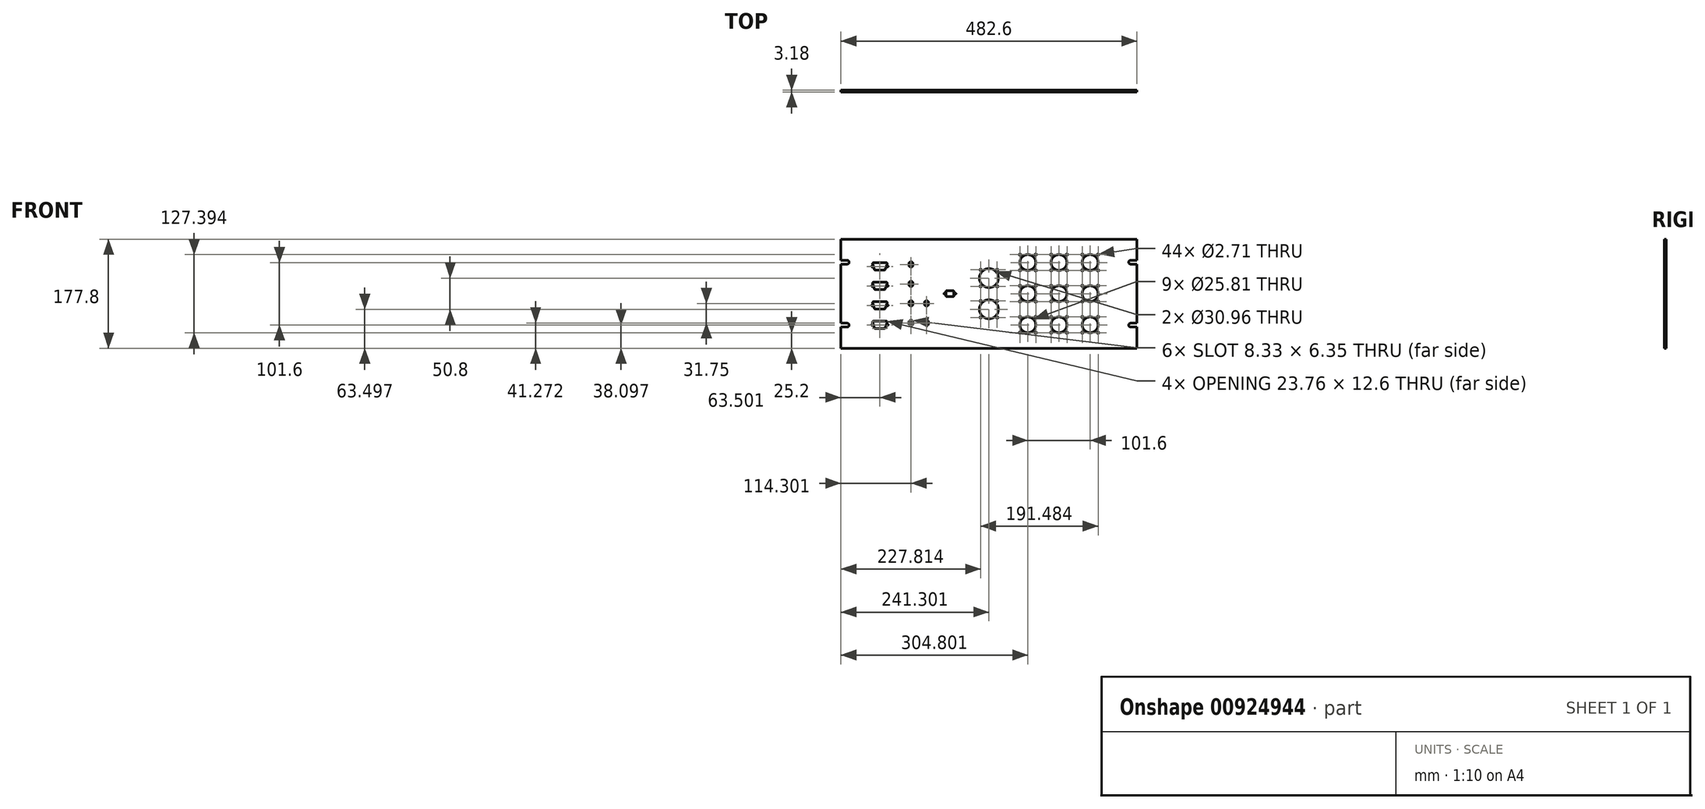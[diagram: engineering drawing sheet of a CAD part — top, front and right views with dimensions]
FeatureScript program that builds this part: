
annotation { "Feature Type Name" : "Feature", "Feature Type Description" : "" }
export const myFeature = defineFeature(function(context is Context, id is Id, definition is map)
    precondition{}
    {
        {
            var Q0;
            Q0=qCreatedBy(makeId("Front.planeOp"),FACE);
            var sketch = newSketch(context, id + "F0", { "sketchPlane" : qUnion([Q0])});
            skLineSegment(sketch, "E0.bottom", {"start": v(-256.05, -152.51) * mm, "end": v(226.55, -152.51) * mm});
            skLineSegment(sketch, "E0.top", {"start": v(-256.05, 25.29) * mm, "end": v(226.55, 25.29) * mm});
            skLineSegment(sketch, "E0.left", {"start": v(-256.05, -152.51) * mm, "end": v(-256.05, -118.1) * mm});
            skLineSegment(sketch, "E0.right", {"start": v(226.55, -152.51) * mm, "end": v(226.55, -118.1) * mm});
            skLineSegment(sketch, "E1", {"start": v(48.75, -99.17) * mm, "end": v(48.75, -129.65) * mm, "construction": true});
            skLineSegment(sketch, "E2", {"start": v(61.45, -114.41) * mm, "end": v(48.75, -114.41) * mm, "construction": true});
            skArc(sketch, "E3", {"start": v(48.75, -101.5) * mm, "mid": v(35.85, -114.41) * mm, "end": v(48.75, -127.32) * mm});
            skPoint(sketch, "E4", {"position": v(36.44, -102.1) * mm});
            skPoint(sketch, "E5", {"position": v(35.26, -100.93) * mm});
            skLineSegment(sketch, "E6", {"start": v(35.26, -100.93) * mm, "end": v(36.44, -102.1) * mm, "construction": true});
            skPoint(sketch, "E7", {"position": v(35.85, -101.52) * mm});
            skPoint(sketch, "E8.MirrorP", {"position": v(61.65, -101.52) * mm});
            skArc(sketch, "E9.MirrorCS", {"start": v(48.75, -101.5) * mm, "mid": v(61.65, -114.41) * mm, "end": v(48.75, -127.32) * mm});
            skPoint(sketch, "E10.MirrorP", {"position": v(35.85, -127.3) * mm});
            skPoint(sketch, "E11.MirrorP", {"position": v(61.65, -127.3) * mm});
            skPoint(sketch, "E12.0.1.0", {"position": v(61.65, -50.72) * mm});
            skLineSegment(sketch, "E12.0.1.1", {"start": v(48.75, -48.37) * mm, "end": v(48.75, -78.85) * mm, "construction": true});
            skPoint(sketch, "E12.0.1.2", {"position": v(36.44, -51.3) * mm});
            skArc(sketch, "E12.0.1.3", {"start": v(48.75, -50.7) * mm, "mid": v(35.85, -63.61) * mm, "end": v(48.75, -76.52) * mm});
            skPoint(sketch, "E12.0.1.4", {"position": v(35.85, -50.72) * mm});
            skArc(sketch, "E12.0.1.5", {"start": v(48.75, -50.7) * mm, "mid": v(61.65, -63.61) * mm, "end": v(48.75, -76.52) * mm});
            skPoint(sketch, "E12.0.1.6", {"position": v(61.65, -76.5) * mm});
            skPoint(sketch, "E12.0.1.7", {"position": v(35.85, -76.5) * mm});
            skLineSegment(sketch, "E12.0.1.8", {"start": v(61.45, -63.61) * mm, "end": v(48.75, -63.61) * mm, "construction": true});
            skPoint(sketch, "E12.0.1.9", {"position": v(35.26, -50.13) * mm});
            skLineSegment(sketch, "E12.0.1.10", {"start": v(35.26, -50.13) * mm, "end": v(36.44, -51.3) * mm, "construction": true});
            skPoint(sketch, "E12.0.2.0", {"position": v(61.65, 0.08) * mm});
            skLineSegment(sketch, "E12.0.2.1", {"start": v(48.75, 2.43) * mm, "end": v(48.75, -28.05) * mm, "construction": true});
            skPoint(sketch, "E12.0.2.2", {"position": v(36.44, -0.5) * mm});
            skArc(sketch, "E12.0.2.3", {"start": v(48.75, 0.1) * mm, "mid": v(35.85, -12.81) * mm, "end": v(48.75, -25.72) * mm});
            skPoint(sketch, "E12.0.2.4", {"position": v(35.85, 0.08) * mm});
            skArc(sketch, "E12.0.2.5", {"start": v(48.75, 0.1) * mm, "mid": v(61.65, -12.81) * mm, "end": v(48.75, -25.72) * mm});
            skPoint(sketch, "E12.0.2.6", {"position": v(61.65, -25.7) * mm});
            skPoint(sketch, "E12.0.2.7", {"position": v(35.85, -25.7) * mm});
            skLineSegment(sketch, "E12.0.2.8", {"start": v(61.45, -12.81) * mm, "end": v(48.75, -12.81) * mm, "construction": true});
            skPoint(sketch, "E12.0.2.9", {"position": v(35.26, 0.67) * mm});
            skLineSegment(sketch, "E12.0.2.10", {"start": v(35.26, 0.67) * mm, "end": v(36.44, -0.5) * mm, "construction": true});
            skPoint(sketch, "E12.1.0.0", {"position": v(112.45, -101.52) * mm});
            skLineSegment(sketch, "E12.1.0.1", {"start": v(99.55, -99.17) * mm, "end": v(99.55, -129.65) * mm, "construction": true});
            skPoint(sketch, "E12.1.0.2", {"position": v(87.24, -102.1) * mm});
            skArc(sketch, "E12.1.0.3", {"start": v(99.55, -101.5) * mm, "mid": v(86.65, -114.41) * mm, "end": v(99.55, -127.32) * mm});
            skPoint(sketch, "E12.1.0.4", {"position": v(86.65, -101.52) * mm});
            skArc(sketch, "E12.1.0.5", {"start": v(99.55, -101.5) * mm, "mid": v(112.45, -114.41) * mm, "end": v(99.55, -127.32) * mm});
            skPoint(sketch, "E12.1.0.6", {"position": v(112.45, -127.3) * mm});
            skPoint(sketch, "E12.1.0.7", {"position": v(86.65, -127.3) * mm});
            skLineSegment(sketch, "E12.1.0.8", {"start": v(112.25, -114.41) * mm, "end": v(99.55, -114.41) * mm, "construction": true});
            skPoint(sketch, "E12.1.0.9", {"position": v(86.06, -100.93) * mm});
            skLineSegment(sketch, "E12.1.0.10", {"start": v(86.06, -100.93) * mm, "end": v(87.24, -102.1) * mm, "construction": true});
            skPoint(sketch, "E12.1.1.0", {"position": v(112.45, -50.72) * mm});
            skLineSegment(sketch, "E12.1.1.1", {"start": v(99.55, -48.37) * mm, "end": v(99.55, -78.85) * mm, "construction": true});
            skPoint(sketch, "E12.1.1.2", {"position": v(87.24, -51.3) * mm});
            skArc(sketch, "E12.1.1.3", {"start": v(99.55, -50.7) * mm, "mid": v(86.65, -63.61) * mm, "end": v(99.55, -76.52) * mm});
            skPoint(sketch, "E12.1.1.4", {"position": v(86.65, -50.72) * mm});
            skArc(sketch, "E12.1.1.5", {"start": v(99.55, -50.7) * mm, "mid": v(112.45, -63.61) * mm, "end": v(99.55, -76.52) * mm});
            skPoint(sketch, "E12.1.1.6", {"position": v(112.45, -76.5) * mm});
            skPoint(sketch, "E12.1.1.7", {"position": v(86.65, -76.5) * mm});
            skLineSegment(sketch, "E12.1.1.8", {"start": v(112.25, -63.61) * mm, "end": v(99.55, -63.61) * mm, "construction": true});
            skPoint(sketch, "E12.1.1.9", {"position": v(86.06, -50.13) * mm});
            skLineSegment(sketch, "E12.1.1.10", {"start": v(86.06, -50.13) * mm, "end": v(87.24, -51.3) * mm, "construction": true});
            skPoint(sketch, "E12.1.2.0", {"position": v(112.45, 0.08) * mm});
            skLineSegment(sketch, "E12.1.2.1", {"start": v(99.55, 2.43) * mm, "end": v(99.55, -28.05) * mm, "construction": true});
            skPoint(sketch, "E12.1.2.2", {"position": v(87.24, -0.5) * mm});
            skArc(sketch, "E12.1.2.3", {"start": v(99.55, 0.1) * mm, "mid": v(86.65, -12.81) * mm, "end": v(99.55, -25.72) * mm});
            skPoint(sketch, "E12.1.2.4", {"position": v(86.65, 0.08) * mm});
            skArc(sketch, "E12.1.2.5", {"start": v(99.55, 0.1) * mm, "mid": v(112.45, -12.81) * mm, "end": v(99.55, -25.72) * mm});
            skPoint(sketch, "E12.1.2.6", {"position": v(112.45, -25.7) * mm});
            skPoint(sketch, "E12.1.2.7", {"position": v(86.65, -25.7) * mm});
            skLineSegment(sketch, "E12.1.2.8", {"start": v(112.25, -12.81) * mm, "end": v(99.55, -12.81) * mm, "construction": true});
            skPoint(sketch, "E12.1.2.9", {"position": v(86.06, 0.67) * mm});
            skLineSegment(sketch, "E12.1.2.10", {"start": v(86.06, 0.67) * mm, "end": v(87.24, -0.5) * mm, "construction": true});
            skPoint(sketch, "E12.2.0.0", {"position": v(163.25, -101.52) * mm});
            skLineSegment(sketch, "E12.2.0.1", {"start": v(150.35, -99.17) * mm, "end": v(150.35, -129.65) * mm, "construction": true});
            skPoint(sketch, "E12.2.0.2", {"position": v(138.04, -102.1) * mm});
            skArc(sketch, "E12.2.0.3", {"start": v(150.35, -101.5) * mm, "mid": v(137.45, -114.41) * mm, "end": v(150.35, -127.32) * mm});
            skPoint(sketch, "E12.2.0.4", {"position": v(137.45, -101.52) * mm});
            skArc(sketch, "E12.2.0.5", {"start": v(150.35, -101.5) * mm, "mid": v(163.25, -114.41) * mm, "end": v(150.35, -127.32) * mm});
            skPoint(sketch, "E12.2.0.6", {"position": v(163.25, -127.3) * mm});
            skPoint(sketch, "E12.2.0.7", {"position": v(137.45, -127.3) * mm});
            skLineSegment(sketch, "E12.2.0.8", {"start": v(163.05, -114.41) * mm, "end": v(150.35, -114.41) * mm, "construction": true});
            skPoint(sketch, "E12.2.0.9", {"position": v(136.86, -100.93) * mm});
            skLineSegment(sketch, "E12.2.0.10", {"start": v(136.86, -100.93) * mm, "end": v(138.04, -102.1) * mm, "construction": true});
            skPoint(sketch, "E12.2.1.0", {"position": v(163.25, -50.72) * mm});
            skLineSegment(sketch, "E12.2.1.1", {"start": v(150.35, -48.37) * mm, "end": v(150.35, -78.85) * mm, "construction": true});
            skPoint(sketch, "E12.2.1.2", {"position": v(138.04, -51.3) * mm});
            skArc(sketch, "E12.2.1.3", {"start": v(150.35, -50.7) * mm, "mid": v(137.45, -63.61) * mm, "end": v(150.35, -76.52) * mm});
            skPoint(sketch, "E12.2.1.4", {"position": v(137.45, -50.72) * mm});
            skArc(sketch, "E12.2.1.5", {"start": v(150.35, -50.7) * mm, "mid": v(163.25, -63.61) * mm, "end": v(150.35, -76.52) * mm});
            skPoint(sketch, "E12.2.1.6", {"position": v(163.25, -76.5) * mm});
            skPoint(sketch, "E12.2.1.7", {"position": v(137.45, -76.5) * mm});
            skLineSegment(sketch, "E12.2.1.8", {"start": v(163.05, -63.61) * mm, "end": v(150.35, -63.61) * mm, "construction": true});
            skPoint(sketch, "E12.2.1.9", {"position": v(136.86, -50.13) * mm});
            skLineSegment(sketch, "E12.2.1.10", {"start": v(136.86, -50.13) * mm, "end": v(138.04, -51.3) * mm, "construction": true});
            skPoint(sketch, "E12.2.2.0", {"position": v(163.25, 0.08) * mm});
            skLineSegment(sketch, "E12.2.2.1", {"start": v(150.35, 2.43) * mm, "end": v(150.35, -28.05) * mm, "construction": true});
            skPoint(sketch, "E12.2.2.2", {"position": v(138.04, -0.5) * mm});
            skArc(sketch, "E12.2.2.3", {"start": v(150.35, 0.1) * mm, "mid": v(137.45, -12.81) * mm, "end": v(150.35, -25.72) * mm});
            skPoint(sketch, "E12.2.2.4", {"position": v(137.45, 0.08) * mm});
            skArc(sketch, "E12.2.2.5", {"start": v(150.35, 0.1) * mm, "mid": v(163.25, -12.81) * mm, "end": v(150.35, -25.72) * mm});
            skPoint(sketch, "E12.2.2.6", {"position": v(163.25, -25.7) * mm});
            skPoint(sketch, "E12.2.2.7", {"position": v(137.45, -25.7) * mm});
            skLineSegment(sketch, "E12.2.2.8", {"start": v(163.05, -12.81) * mm, "end": v(150.35, -12.81) * mm, "construction": true});
            skPoint(sketch, "E12.2.2.9", {"position": v(136.86, 0.67) * mm});
            skLineSegment(sketch, "E12.2.2.10", {"start": v(136.86, 0.67) * mm, "end": v(138.04, -0.5) * mm, "construction": true});
            skLineSegment(sketch, "E12.direction1", {"start": v(35.85, -127.3) * mm, "end": v(86.65, -127.3) * mm, "construction": true});
            skLineSegment(sketch, "E12.direction2", {"start": v(35.85, -127.3) * mm, "end": v(35.85, -76.5) * mm, "construction": true});
            skPoint(sketch, "E13", {"position": v(-245.76, -12.3) * mm});
            skLineSegment(sketch, "E14", {"start": v(-256.05, -63.61) * mm, "end": v(-239.44, -63.61) * mm, "construction": true});
            skLineSegment(sketch, "E15", {"start": v(-14.75, 38.2) * mm, "end": v(-14.75, 25.29) * mm, "construction": true});
            skLineSegment(sketch, "E16", {"start": v(-245.76, -12.3) * mm, "end": v(-256.05, -12.3) * mm, "construction": true});
            skArc(sketch, "E17.0.startCap", {"start": v(-245.76, -9.13) * mm, "mid": v(-242.59, -12.3) * mm, "end": v(-245.76, -15.48) * mm});
            skLineSegment(sketch, "E17.0.left", {"start": v(-245.76, -15.48) * mm, "end": v(-256.05, -15.48) * mm});
            skLineSegment(sketch, "E17.0.right", {"start": v(-245.76, -9.13) * mm, "end": v(-256.05, -9.13) * mm});
            skLineSegment(sketch, "E18.trimOffspring", {"start": v(-256.05, -9.13) * mm, "end": v(-256.05, 25.29) * mm});
            skArc(sketch, "E19.MirrorCS", {"start": v(-245.76, -118.1) * mm, "mid": v(-242.59, -114.92) * mm, "end": v(-245.76, -111.75) * mm});
            skLineSegment(sketch, "E20.MirrorCS", {"start": v(-245.76, -111.75) * mm, "end": v(-256.05, -111.75) * mm});
            skLineSegment(sketch, "E21.MirrorCS", {"start": v(-256.05, -118.1) * mm, "end": v(-256.05, -152.51) * mm});
            skLineSegment(sketch, "E22.MirrorCS", {"start": v(-245.76, -118.1) * mm, "end": v(-256.05, -118.1) * mm});
            skLineSegment(sketch, "E23.trimOffspring", {"start": v(-256.05, -111.75) * mm, "end": v(-256.05, -15.48) * mm});
            skArc(sketch, "E24.MirrorCS", {"start": v(216.26, -9.13) * mm, "mid": v(213.09, -12.3) * mm, "end": v(216.26, -15.48) * mm});
            skLineSegment(sketch, "E25.MirrorCS", {"start": v(216.26, -15.48) * mm, "end": v(226.55, -15.48) * mm});
            skLineSegment(sketch, "E26.MirrorCS", {"start": v(216.26, -9.13) * mm, "end": v(226.55, -9.13) * mm});
            skLineSegment(sketch, "E27.MirrorCS", {"start": v(216.26, -111.75) * mm, "end": v(226.55, -111.75) * mm});
            skArc(sketch, "E28.MirrorCS", {"start": v(216.26, -118.1) * mm, "mid": v(213.09, -114.92) * mm, "end": v(216.26, -111.75) * mm});
            skLineSegment(sketch, "E29.MirrorCS", {"start": v(216.26, -118.1) * mm, "end": v(226.55, -118.1) * mm});
            skLineSegment(sketch, "E30.trimOffspring", {"start": v(226.55, -9.13) * mm, "end": v(226.55, 25.29) * mm});
            skLineSegment(sketch, "E31.trimOffspring", {"start": v(226.55, -111.75) * mm, "end": v(226.55, -15.48) * mm});
            skLineSegment(sketch, "E32", {"start": v(-205.05, -114.41) * mm, "end": v(-180.05, -114.41) * mm, "construction": true});
            skLineSegment(sketch, "E33", {"start": v(-192.55, -118.22) * mm, "end": v(-192.55, -110.6) * mm, "construction": true});
            skPoint(sketch, "E33.startSnap0", {"position": v(-192.55, -114.41) * mm});
            skLineSegment(sketch, "E34", {"start": v(-192.55, -106.3) * mm, "end": v(-192.55, -106.3) * mm});
            skLineSegment(sketch, "E35", {"start": v(-192.55, -118) * mm, "end": v(-192.55, -118) * mm});
            skLineSegment(sketch, "E36", {"start": v(-204.33, -110.87) * mm, "end": v(-201.61, -119.26) * mm});
            skLineSegment(sketch, "E37", {"start": v(-180.76, -110.87) * mm, "end": v(-183.49, -119.26) * mm});
            skLineSegment(sketch, "E38", {"start": v(-202.33, -108.11) * mm, "end": v(-182.77, -108.11) * mm});
            skLineSegment(sketch, "E39", {"start": v(-199.6, -120.71) * mm, "end": v(-185.5, -120.71) * mm});
            skLineSegment(sketch, "E40", {"start": v(-192.55, -108.11) * mm, "end": v(-192.55, -104.89) * mm, "construction": true});
            skLineSegment(sketch, "E41", {"start": v(-192.55, -120.71) * mm, "end": v(-192.55, -122.22) * mm, "construction": true});
            skArc(sketch, "E42", {"start": v(-202.33, -108.11) * mm, "mid": v(-204.03, -108.98) * mm, "end": v(-204.33, -110.87) * mm});
            skArc(sketch, "E43", {"start": v(-180.76, -110.87) * mm, "mid": v(-181.06, -108.98) * mm, "end": v(-182.77, -108.11) * mm});
            skArc(sketch, "E44", {"start": v(-185.5, -120.71) * mm, "mid": v(-184.25, -120.3) * mm, "end": v(-183.49, -119.26) * mm});
            skArc(sketch, "E45", {"start": v(-201.61, -119.26) * mm, "mid": v(-200.85, -120.3) * mm, "end": v(-199.6, -120.71) * mm});
            skLineSegment(sketch, "E46.direction1", {"start": v(-188.91, -123.4) * mm, "end": v(-163.51, -123.4) * mm, "construction": true});
            skLineSegment(sketch, "E46.direction2", {"start": v(-188.91, -123.4) * mm, "end": v(-188.91, -91.66) * mm, "construction": true});
            skArc(sketch, "E47", {"start": v(-138.57, -108.54) * mm, "mid": v(-141.75, -107.07) * mm, "end": v(-144.92, -108.54) * mm});
            skLineSegment(sketch, "E48.left", {"start": v(-138.57, -113.93) * mm, "end": v(-138.57, -108.54) * mm});
            skLineSegment(sketch, "E48.right", {"start": v(-144.92, -113.93) * mm, "end": v(-144.92, -108.54) * mm});
            skArc(sketch, "E49.trimOffspring", {"start": v(-144.92, -113.93) * mm, "mid": v(-141.75, -115.4) * mm, "end": v(-138.57, -113.93) * mm});
            skArc(sketch, "E50.0.1.0", {"start": v(-138.57, -76.8) * mm, "mid": v(-141.75, -75.32) * mm, "end": v(-144.92, -76.8) * mm});
            skArc(sketch, "E50.0.1.1", {"start": v(-144.92, -82.18) * mm, "mid": v(-141.75, -83.65) * mm, "end": v(-138.57, -82.18) * mm});
            skPoint(sketch, "E50.0.1.2", {"position": v(-141.75, -79.49) * mm});
            skLineSegment(sketch, "E50.0.1.3", {"start": v(-138.57, -82.18) * mm, "end": v(-138.57, -76.8) * mm});
            skLineSegment(sketch, "E50.0.1.4", {"start": v(-144.92, -82.18) * mm, "end": v(-144.92, -76.8) * mm});
            skArc(sketch, "E50.0.2.0", {"start": v(-138.57, -45.04) * mm, "mid": v(-141.75, -43.57) * mm, "end": v(-144.92, -45.04) * mm});
            skArc(sketch, "E50.0.2.1", {"start": v(-144.92, -50.43) * mm, "mid": v(-141.75, -51.9) * mm, "end": v(-138.57, -50.43) * mm});
            skPoint(sketch, "E50.0.2.2", {"position": v(-141.75, -47.74) * mm});
            skLineSegment(sketch, "E50.0.2.3", {"start": v(-138.57, -50.43) * mm, "end": v(-138.57, -45.04) * mm});
            skLineSegment(sketch, "E50.0.2.4", {"start": v(-144.92, -50.43) * mm, "end": v(-144.92, -45.04) * mm});
            skArc(sketch, "E50.0.3.0", {"start": v(-138.57, -13.3) * mm, "mid": v(-141.75, -11.82) * mm, "end": v(-144.92, -13.3) * mm});
            skArc(sketch, "E50.0.3.1", {"start": v(-144.92, -18.68) * mm, "mid": v(-141.75, -20.15) * mm, "end": v(-138.57, -18.68) * mm});
            skPoint(sketch, "E50.0.3.2", {"position": v(-141.75, -15.99) * mm});
            skLineSegment(sketch, "E50.0.3.3", {"start": v(-138.57, -18.68) * mm, "end": v(-138.57, -13.3) * mm});
            skLineSegment(sketch, "E50.0.3.4", {"start": v(-144.92, -18.68) * mm, "end": v(-144.92, -13.3) * mm});
            skLineSegment(sketch, "E50.direction1", {"start": v(-144.92, -113.93) * mm, "end": v(-119.52, -113.93) * mm, "construction": true});
            skLineSegment(sketch, "E50.direction2", {"start": v(-144.92, -113.93) * mm, "end": v(-144.92, -82.18) * mm, "construction": true});
            skLineSegment(sketch, "E51", {"start": v(-141.75, -47.74) * mm, "end": v(-141.75, -79.49) * mm, "construction": true});
            skLineSegment(sketch, "E52", {"start": v(-141.75, -63.61) * mm, "end": v(-151.51, -63.61) * mm, "construction": true});
            skLineSegment(sketch, "E53.0.0.1", {"start": v(-199.6, -88.96) * mm, "end": v(-185.5, -88.96) * mm});
            skLineSegment(sketch, "E53.3.0.1", {"start": v(-180.76, -79.12) * mm, "end": v(-183.49, -87.5) * mm});
            skArc(sketch, "E53.6.0.1", {"start": v(-202.33, -76.36) * mm, "mid": v(-204.03, -77.23) * mm, "end": v(-204.33, -79.12) * mm});
            skLineSegment(sketch, "E53.10.0.1", {"start": v(-205.05, -82.66) * mm, "end": v(-180.05, -82.66) * mm, "construction": true});
            skLineSegment(sketch, "E53.13.0.1", {"start": v(-202.33, -76.36) * mm, "end": v(-182.77, -76.36) * mm});
            skArc(sketch, "E53.16.0.1", {"start": v(-180.76, -79.12) * mm, "mid": v(-181.06, -77.23) * mm, "end": v(-182.77, -76.36) * mm});
            skLineSegment(sketch, "E53.20.0.1", {"start": v(-204.33, -79.12) * mm, "end": v(-201.61, -87.5) * mm});
            skLineSegment(sketch, "E53.23.0.1", {"start": v(-192.55, -76.36) * mm, "end": v(-192.55, -73.14) * mm, "construction": true});
            skLineSegment(sketch, "E53.26.0.1", {"start": v(-192.55, -86.47) * mm, "end": v(-192.55, -78.85) * mm, "construction": true});
            skPoint(sketch, "E53.29.0.1", {"position": v(-192.55, -82.66) * mm});
            skArc(sketch, "E53.30.0.1", {"start": v(-185.5, -88.96) * mm, "mid": v(-184.25, -88.56) * mm, "end": v(-183.49, -87.5) * mm});
            skLineSegment(sketch, "E53.34.0.1", {"start": v(-192.55, -88.96) * mm, "end": v(-192.55, -90.47) * mm, "construction": true});
            skArc(sketch, "E53.37.0.1", {"start": v(-201.61, -87.5) * mm, "mid": v(-200.85, -88.56) * mm, "end": v(-199.6, -88.96) * mm});
            skLineSegment(sketch, "E53.0.0.2", {"start": v(-199.6, -57.21) * mm, "end": v(-185.5, -57.21) * mm});
            skLineSegment(sketch, "E53.3.0.2", {"start": v(-180.76, -47.37) * mm, "end": v(-183.49, -55.76) * mm});
            skArc(sketch, "E53.6.0.2", {"start": v(-202.33, -44.61) * mm, "mid": v(-204.03, -45.48) * mm, "end": v(-204.33, -47.37) * mm});
            skLineSegment(sketch, "E53.10.0.2", {"start": v(-205.05, -50.91) * mm, "end": v(-180.05, -50.91) * mm, "construction": true});
            skLineSegment(sketch, "E53.13.0.2", {"start": v(-202.33, -44.61) * mm, "end": v(-182.77, -44.61) * mm});
            skArc(sketch, "E53.16.0.2", {"start": v(-180.76, -47.37) * mm, "mid": v(-181.06, -45.48) * mm, "end": v(-182.77, -44.61) * mm});
            skLineSegment(sketch, "E53.20.0.2", {"start": v(-204.33, -47.37) * mm, "end": v(-201.61, -55.76) * mm});
            skLineSegment(sketch, "E53.23.0.2", {"start": v(-192.55, -44.61) * mm, "end": v(-192.55, -41.39) * mm, "construction": true});
            skLineSegment(sketch, "E53.26.0.2", {"start": v(-192.55, -54.72) * mm, "end": v(-192.55, -47.1) * mm, "construction": true});
            skPoint(sketch, "E53.29.0.2", {"position": v(-192.55, -50.91) * mm});
            skArc(sketch, "E53.30.0.2", {"start": v(-185.5, -57.21) * mm, "mid": v(-184.25, -56.8) * mm, "end": v(-183.49, -55.76) * mm});
            skLineSegment(sketch, "E53.34.0.2", {"start": v(-192.55, -57.21) * mm, "end": v(-192.55, -58.72) * mm, "construction": true});
            skArc(sketch, "E53.37.0.2", {"start": v(-201.61, -55.76) * mm, "mid": v(-200.85, -56.8) * mm, "end": v(-199.6, -57.21) * mm});
            skLineSegment(sketch, "E53.0.0.3", {"start": v(-199.6, -25.46) * mm, "end": v(-185.5, -25.46) * mm});
            skLineSegment(sketch, "E53.3.0.3", {"start": v(-180.76, -15.62) * mm, "end": v(-183.49, -24) * mm});
            skArc(sketch, "E53.6.0.3", {"start": v(-202.33, -12.86) * mm, "mid": v(-204.03, -13.73) * mm, "end": v(-204.33, -15.62) * mm});
            skLineSegment(sketch, "E53.10.0.3", {"start": v(-205.05, -19.16) * mm, "end": v(-180.05, -19.16) * mm, "construction": true});
            skLineSegment(sketch, "E53.13.0.3", {"start": v(-202.33, -12.86) * mm, "end": v(-182.77, -12.86) * mm});
            skArc(sketch, "E53.16.0.3", {"start": v(-180.76, -15.62) * mm, "mid": v(-181.06, -13.73) * mm, "end": v(-182.77, -12.86) * mm});
            skLineSegment(sketch, "E53.20.0.3", {"start": v(-204.33, -15.62) * mm, "end": v(-201.61, -24) * mm});
            skLineSegment(sketch, "E53.23.0.3", {"start": v(-192.55, -12.86) * mm, "end": v(-192.55, -9.64) * mm, "construction": true});
            skLineSegment(sketch, "E53.26.0.3", {"start": v(-192.55, -22.97) * mm, "end": v(-192.55, -15.35) * mm, "construction": true});
            skPoint(sketch, "E53.29.0.3", {"position": v(-192.55, -19.16) * mm});
            skArc(sketch, "E53.30.0.3", {"start": v(-185.5, -25.46) * mm, "mid": v(-184.25, -25.06) * mm, "end": v(-183.49, -24) * mm});
            skLineSegment(sketch, "E53.34.0.3", {"start": v(-192.55, -25.46) * mm, "end": v(-192.55, -26.97) * mm, "construction": true});
            skArc(sketch, "E53.37.0.3", {"start": v(-201.61, -24) * mm, "mid": v(-200.85, -25.06) * mm, "end": v(-199.6, -25.46) * mm});
            skLineSegment(sketch, "E54.bottom", {"start": v(-1.26, -102.5) * mm, "end": v(-28.24, -102.5) * mm, "construction": true});
            skLineSegment(sketch, "E54.top", {"start": v(-1.26, -75.53) * mm, "end": v(-28.24, -75.53) * mm, "construction": true});
            skLineSegment(sketch, "E54.left", {"start": v(-1.26, -102.5) * mm, "end": v(-1.26, -75.53) * mm, "construction": true});
            skLineSegment(sketch, "E54.right", {"start": v(-28.24, -102.5) * mm, "end": v(-28.24, -75.53) * mm, "construction": true});
            skPoint(sketch, "E54.middle", {"position": v(-14.75, -89.01) * mm});
            skCircle(sketch, "E55", {"center": v(-14.75, -89.01) * mm, "radius": 15.48 * mm});
            skCircle(sketch, "E56.0.1.0", {"center": v(-14.75, -38.21) * mm, "radius": 15.48 * mm});
            skPoint(sketch, "E56.0.1.1", {"position": v(-14.75, -38.21) * mm});
            skLineSegment(sketch, "E56.0.1.2", {"start": v(-28.24, -51.7) * mm, "end": v(-28.24, -24.73) * mm, "construction": true});
            skLineSegment(sketch, "E56.0.1.3", {"start": v(-1.26, -51.7) * mm, "end": v(-1.26, -24.73) * mm, "construction": true});
            skLineSegment(sketch, "E56.0.1.4", {"start": v(-1.26, -51.7) * mm, "end": v(-28.24, -51.7) * mm, "construction": true});
            skLineSegment(sketch, "E56.0.1.5", {"start": v(-1.26, -24.73) * mm, "end": v(-28.24, -24.73) * mm, "construction": true});
            skLineSegment(sketch, "E56.direction1", {"start": v(-80.15, -102.5) * mm, "end": v(-28.24, -102.5) * mm, "construction": true});
            skLineSegment(sketch, "E56.direction2", {"start": v(-28.24, -102.5) * mm, "end": v(-28.24, -51.7) * mm, "construction": true});
            skLineSegment(sketch, "E57", {"start": v(-14.75, -38.21) * mm, "end": v(-14.75, -89.01) * mm, "construction": true});
            skLineSegment(sketch, "E58", {"start": v(-12.7, -63.61) * mm, "end": v(-14.75, -63.61) * mm, "construction": true});
            skLineSegment(sketch, "E59.bottom", {"start": v(-72.25, -68.36) * mm, "end": v(-84.24, -68.36) * mm});
            skLineSegment(sketch, "E59.top", {"start": v(-72.25, -58.86) * mm, "end": v(-84.24, -58.86) * mm});
            skLineSegment(sketch, "E59.left", {"start": v(-71.75, -67.85) * mm, "end": v(-71.75, -59.37) * mm});
            skLineSegment(sketch, "E59.right", {"start": v(-84.75, -67.85) * mm, "end": v(-84.75, -59.37) * mm});
            skPoint(sketch, "E59.middle", {"position": v(-78.25, -63.61) * mm});
            skLineSegment(sketch, "E60", {"start": v(-87.25, -63.61) * mm, "end": v(-69.24, -63.61) * mm, "construction": true});
            skPoint(sketch, "E61.visualSharp", {"position": v(-84.75, -58.86) * mm});
            skArc(sketch, "E61.filletArc", {"start": v(-84.24, -58.86) * mm, "mid": v(-84.6, -59.01) * mm, "end": v(-84.75, -59.37) * mm});
            skPoint(sketch, "E62.visualSharp", {"position": v(-71.75, -58.86) * mm});
            skArc(sketch, "E62.filletArc", {"start": v(-71.75, -59.37) * mm, "mid": v(-71.9, -59.01) * mm, "end": v(-72.25, -58.86) * mm});
            skPoint(sketch, "E63.visualSharp", {"position": v(-71.75, -68.36) * mm});
            skArc(sketch, "E63.filletArc", {"start": v(-72.25, -68.36) * mm, "mid": v(-71.9, -68.21) * mm, "end": v(-71.75, -67.85) * mm});
            skPoint(sketch, "E64.visualSharp", {"position": v(-84.75, -68.36) * mm});
            skArc(sketch, "E64.filletArc", {"start": v(-84.75, -67.85) * mm, "mid": v(-84.6, -68.21) * mm, "end": v(-84.24, -68.36) * mm});
            skArc(sketch, "E65.0.1.0", {"start": v(-113.17, -108.54) * mm, "mid": v(-116.35, -107.07) * mm, "end": v(-119.52, -108.54) * mm});
            skArc(sketch, "E65.4.1.0", {"start": v(-119.52, -113.93) * mm, "mid": v(-116.35, -115.4) * mm, "end": v(-113.17, -113.93) * mm});
            skPoint(sketch, "E65.8.1.0", {"position": v(-116.35, -111.24) * mm});
            skLineSegment(sketch, "E65.9.1.0", {"start": v(-113.17, -113.93) * mm, "end": v(-113.17, -108.54) * mm});
            skLineSegment(sketch, "E65.12.1.0", {"start": v(-119.52, -113.93) * mm, "end": v(-119.52, -108.54) * mm});
            skArc(sketch, "E65.0.1.1", {"start": v(-113.17, -76.8) * mm, "mid": v(-116.35, -75.32) * mm, "end": v(-119.52, -76.8) * mm});
            skArc(sketch, "E65.4.1.1", {"start": v(-119.52, -82.18) * mm, "mid": v(-116.35, -83.65) * mm, "end": v(-113.17, -82.18) * mm});
            skPoint(sketch, "E65.8.1.1", {"position": v(-116.35, -79.49) * mm});
            skLineSegment(sketch, "E65.9.1.1", {"start": v(-113.17, -82.18) * mm, "end": v(-113.17, -76.8) * mm});
            skLineSegment(sketch, "E65.12.1.1", {"start": v(-119.52, -82.18) * mm, "end": v(-119.52, -76.8) * mm});
            skSolve(sketch);
        }
        {
            var Q0;
            Q0=qSketchRegion(id+"F0",true);
            extrude(context, id + "F1", {"entities" : qUnion([Q0]), "depth" : 3.17 * mm, "offsetDistance" : 25.4 * mm});
        }
        {
            var Q0;
            Q0=sQuery(id+"F0.wireOp",VERTEX,"E12.0.2.4");
            var Q1;
            Q1=sQuery(id+"F0.wireOp",VERTEX,"E12.0.2.0");
            var Q2;
            Q2=sQuery(id+"F0.wireOp",VERTEX,"E12.0.2.6");
            var Q3;
            Q3=sQuery(id+"F0.wireOp",VERTEX,"E12.0.2.7");
            var Q4;
            Q4=sQuery(id+"F0.wireOp",VERTEX,"E12.1.2.7");
            var Q5;
            Q5=sQuery(id+"F0.wireOp",VERTEX,"E12.1.2.6");
            var Q6;
            Q6=sQuery(id+"F0.wireOp",VERTEX,"E12.1.2.0");
            var Q7;
            Q7=sQuery(id+"F0.wireOp",VERTEX,"E12.1.2.4");
            var Q8;
            Q8=sQuery(id+"F0.wireOp",VERTEX,"E12.0.1.4");
            var Q9;
            Q9=sQuery(id+"F0.wireOp",VERTEX,"E12.0.1.0");
            var Q10;
            Q10=sQuery(id+"F0.wireOp",VERTEX,"E12.1.1.4");
            var Q11;
            Q11=sQuery(id+"F0.wireOp",VERTEX,"E12.1.1.0");
            var Q12;
            Q12=sQuery(id+"F0.wireOp",VERTEX,"E12.2.2.4");
            var Q13;
            Q13=sQuery(id+"F0.wireOp",VERTEX,"E12.2.2.0");
            var Q14;
            Q14=sQuery(id+"F0.wireOp",VERTEX,"E12.2.2.6");
            var Q15;
            Q15=sQuery(id+"F0.wireOp",VERTEX,"E12.2.2.7");
            var Q16;
            Q16=sQuery(id+"F0.wireOp",VERTEX,"E12.2.1.4");
            var Q17;
            Q17=sQuery(id+"F0.wireOp",VERTEX,"E12.2.1.0");
            var Q18;
            Q18=sQuery(id+"F0.wireOp",VERTEX,"E12.0.1.7");
            var Q19;
            Q19=sQuery(id+"F0.wireOp",VERTEX,"E12.0.1.6");
            var Q20;
            Q20=sQuery(id+"F0.wireOp",VERTEX,"E12.1.1.7");
            var Q21;
            Q21=sQuery(id+"F0.wireOp",VERTEX,"E12.1.1.6");
            var Q22;
            Q22=sQuery(id+"F0.wireOp",VERTEX,"E12.2.1.7");
            var Q23;
            Q23=sQuery(id+"F0.wireOp",VERTEX,"E12.2.1.6");
            var Q24;
            Q24=sQuery(id+"F0.wireOp",VERTEX,"E12.2.0.0");
            var Q25;
            Q25=sQuery(id+"F0.wireOp",VERTEX,"E12.2.0.4");
            var Q26;
            Q26=sQuery(id+"F0.wireOp",VERTEX,"E12.1.0.0");
            var Q27;
            Q27=sQuery(id+"F0.wireOp",VERTEX,"E12.1.0.4");
            var Q28;
            Q28=sQuery(id+"F0.wireOp",VERTEX,"E8.MirrorP");
            var Q29;
            Q29=sQuery(id+"F0.wireOp",VERTEX,"E7");
            var Q30;
            Q30=sQuery(id+"F0.wireOp",VERTEX,"E10.MirrorP");
            var Q31;
            Q31=sQuery(id+"F0.wireOp",VERTEX,"E11.MirrorP");
            var Q32;
            Q32=sQuery(id+"F0.wireOp",VERTEX,"E12.1.0.7");
            var Q33;
            Q33=sQuery(id+"F0.wireOp",VERTEX,"E12.1.0.6");
            var Q34;
            Q34=sQuery(id+"F0.wireOp",VERTEX,"E12.2.0.7");
            var Q35;
            Q35=sQuery(id+"F0.wireOp",VERTEX,"E12.2.0.6");
            var Q36;
            Q36=makeQuery(id+"F1.opExtrude","SWEPT_BODY",BODY,{"disambiguationData":[OSD([sQuery(id+"F0.wireOp",EDGE,"E0.bottom"),sQuery(id+"F0.wireOp",EDGE,"E0.top"),sQuery(id+"F0.wireOp",EDGE,"E0.left"),sQuery(id+"F0.wireOp",EDGE,"E0.right"),sQuery(id+"F0.wireOp",EDGE,"b0d6a3e9-dda7-4b39-bde3-1ef797a92e78"),sQuery(id+"F0.wireOp",EDGE,"de29c7d1-a9bf-4cad-87a4-eb185ccb766c"),sQuery(id+"F0.wireOp",EDGE,"d8eac7f8-13a5-4df2-9675-793bb3d629a8"),sQuery(id+"F0.wireOp",EDGE,"9a60e7e6-8b1c-49ce-a587-7fef7e458512"),sQuery(id+"F0.wireOp",EDGE,"f7618abf-457f-4771-8f9e-37748c564853"),sQuery(id+"F0.wireOp",EDGE,"12616632-bdf5-4fef-91ed-fab7e749e060"),sQuery(id+"F0.wireOp",EDGE,"a72d509d-39ea-4c83-8068-937b1f15b5a1"),sQuery(id+"F0.wireOp",EDGE,"b72412ee-4e9a-4b00-b16c-6c6999a1730f"),sQuery(id+"F0.wireOp",EDGE,"7d2e699d-989a-44b9-9e27-5967113c99a9"),sQuery(id+"F0.wireOp",EDGE,"4471e13d-aa83-4026-a50f-020390fa38f4"),sQuery(id+"F0.wireOp",EDGE,"1e7b34f2-0b9f-4ddf-89ed-3da1b662023f.0.1.1"),sQuery(id+"F0.wireOp",EDGE,"1e7b34f2-0b9f-4ddf-89ed-3da1b662023f.0.1.2"),sQuery(id+"F0.wireOp",EDGE,"1e7b34f2-0b9f-4ddf-89ed-3da1b662023f.0.1.3"),sQuery(id+"F0.wireOp",EDGE,"1e7b34f2-0b9f-4ddf-89ed-3da1b662023f.0.1.4"),sQuery(id+"F0.wireOp",EDGE,"1e7b34f2-0b9f-4ddf-89ed-3da1b662023f.0.1.8"),sQuery(id+"F0.wireOp",EDGE,"1e7b34f2-0b9f-4ddf-89ed-3da1b662023f.0.1.12"),sQuery(id+"F0.wireOp",EDGE,"1e7b34f2-0b9f-4ddf-89ed-3da1b662023f.0.1.13"),sQuery(id+"F0.wireOp",EDGE,"1e7b34f2-0b9f-4ddf-89ed-3da1b662023f.0.1.14"),sQuery(id+"F0.wireOp",EDGE,"1e7b34f2-0b9f-4ddf-89ed-3da1b662023f.0.1.15"),sQuery(id+"F0.wireOp",EDGE,"1e7b34f2-0b9f-4ddf-89ed-3da1b662023f.0.1.16"),sQuery(id+"F0.wireOp",EDGE,"1e7b34f2-0b9f-4ddf-89ed-3da1b662023f.0.2.1"),sQuery(id+"F0.wireOp",EDGE,"1e7b34f2-0b9f-4ddf-89ed-3da1b662023f.0.2.2"),sQuery(id+"F0.wireOp",EDGE,"1e7b34f2-0b9f-4ddf-89ed-3da1b662023f.0.2.3"),sQuery(id+"F0.wireOp",EDGE,"1e7b34f2-0b9f-4ddf-89ed-3da1b662023f.0.2.4"),sQuery(id+"F0.wireOp",EDGE,"1e7b34f2-0b9f-4ddf-89ed-3da1b662023f.0.2.8"),sQuery(id+"F0.wireOp",EDGE,"1e7b34f2-0b9f-4ddf-89ed-3da1b662023f.0.2.12"),sQuery(id+"F0.wireOp",EDGE,"1e7b34f2-0b9f-4ddf-89ed-3da1b662023f.0.2.13"),sQuery(id+"F0.wireOp",EDGE,"1e7b34f2-0b9f-4ddf-89ed-3da1b662023f.0.2.14"),sQuery(id+"F0.wireOp",EDGE,"1e7b34f2-0b9f-4ddf-89ed-3da1b662023f.0.2.15"),sQuery(id+"F0.wireOp",EDGE,"1e7b34f2-0b9f-4ddf-89ed-3da1b662023f.0.2.16"),sQuery(id+"F0.wireOp",EDGE,"1e7b34f2-0b9f-4ddf-89ed-3da1b662023f.0.3.1"),sQuery(id+"F0.wireOp",EDGE,"1e7b34f2-0b9f-4ddf-89ed-3da1b662023f.0.3.2"),sQuery(id+"F0.wireOp",EDGE,"1e7b34f2-0b9f-4ddf-89ed-3da1b662023f.0.3.3"),sQuery(id+"F0.wireOp",EDGE,"1e7b34f2-0b9f-4ddf-89ed-3da1b662023f.0.3.4"),sQuery(id+"F0.wireOp",EDGE,"1e7b34f2-0b9f-4ddf-89ed-3da1b662023f.0.3.8"),sQuery(id+"F0.wireOp",EDGE,"1e7b34f2-0b9f-4ddf-89ed-3da1b662023f.0.3.12"),sQuery(id+"F0.wireOp",EDGE,"1e7b34f2-0b9f-4ddf-89ed-3da1b662023f.0.3.13"),sQuery(id+"F0.wireOp",EDGE,"1e7b34f2-0b9f-4ddf-89ed-3da1b662023f.0.3.14"),sQuery(id+"F0.wireOp",EDGE,"1e7b34f2-0b9f-4ddf-89ed-3da1b662023f.0.3.15"),sQuery(id+"F0.wireOp",EDGE,"1e7b34f2-0b9f-4ddf-89ed-3da1b662023f.0.3.16"),sQuery(id+"F0.wireOp",EDGE,"1e7b34f2-0b9f-4ddf-89ed-3da1b662023f.0.4.1"),sQuery(id+"F0.wireOp",EDGE,"1e7b34f2-0b9f-4ddf-89ed-3da1b662023f.0.4.2"),sQuery(id+"F0.wireOp",EDGE,"1e7b34f2-0b9f-4ddf-89ed-3da1b662023f.0.4.3"),sQuery(id+"F0.wireOp",EDGE,"1e7b34f2-0b9f-4ddf-89ed-3da1b662023f.0.4.4"),sQuery(id+"F0.wireOp",EDGE,"1e7b34f2-0b9f-4ddf-89ed-3da1b662023f.0.4.8"),sQuery(id+"F0.wireOp",EDGE,"1e7b34f2-0b9f-4ddf-89ed-3da1b662023f.0.4.12"),sQuery(id+"F0.wireOp",EDGE,"1e7b34f2-0b9f-4ddf-89ed-3da1b662023f.0.4.13"),sQuery(id+"F0.wireOp",EDGE,"1e7b34f2-0b9f-4ddf-89ed-3da1b662023f.0.4.14"),sQuery(id+"F0.wireOp",EDGE,"1e7b34f2-0b9f-4ddf-89ed-3da1b662023f.0.4.15"),sQuery(id+"F0.wireOp",EDGE,"1e7b34f2-0b9f-4ddf-89ed-3da1b662023f.0.4.16"),sQuery(id+"F0.wireOp",EDGE,"1e7b34f2-0b9f-4ddf-89ed-3da1b662023f.0.5.1"),sQuery(id+"F0.wireOp",EDGE,"1e7b34f2-0b9f-4ddf-89ed-3da1b662023f.0.5.2"),sQuery(id+"F0.wireOp",EDGE,"1e7b34f2-0b9f-4ddf-89ed-3da1b662023f.0.5.3"),sQuery(id+"F0.wireOp",EDGE,"1e7b34f2-0b9f-4ddf-89ed-3da1b662023f.0.5.4"),sQuery(id+"F0.wireOp",EDGE,"1e7b34f2-0b9f-4ddf-89ed-3da1b662023f.0.5.8"),sQuery(id+"F0.wireOp",EDGE,"1e7b34f2-0b9f-4ddf-89ed-3da1b662023f.0.5.12"),sQuery(id+"F0.wireOp",EDGE,"1e7b34f2-0b9f-4ddf-89ed-3da1b662023f.0.5.13"),sQuery(id+"F0.wireOp",EDGE,"1e7b34f2-0b9f-4ddf-89ed-3da1b662023f.0.5.14"),sQuery(id+"F0.wireOp",EDGE,"1e7b34f2-0b9f-4ddf-89ed-3da1b662023f.0.5.15"),sQuery(id+"F0.wireOp",EDGE,"1e7b34f2-0b9f-4ddf-89ed-3da1b662023f.0.5.16"),sQuery(id+"F0.wireOp",EDGE,"1e7b34f2-0b9f-4ddf-89ed-3da1b662023f.0.6.1"),sQuery(id+"F0.wireOp",EDGE,"1e7b34f2-0b9f-4ddf-89ed-3da1b662023f.0.6.2"),sQuery(id+"F0.wireOp",EDGE,"1e7b34f2-0b9f-4ddf-89ed-3da1b662023f.0.6.3"),sQuery(id+"F0.wireOp",EDGE,"1e7b34f2-0b9f-4ddf-89ed-3da1b662023f.0.6.4"),sQuery(id+"F0.wireOp",EDGE,"1e7b34f2-0b9f-4ddf-89ed-3da1b662023f.0.6.8"),sQuery(id+"F0.wireOp",EDGE,"1e7b34f2-0b9f-4ddf-89ed-3da1b662023f.0.6.12"),sQuery(id+"F0.wireOp",EDGE,"1e7b34f2-0b9f-4ddf-89ed-3da1b662023f.0.6.13"),sQuery(id+"F0.wireOp",EDGE,"1e7b34f2-0b9f-4ddf-89ed-3da1b662023f.0.6.14"),sQuery(id+"F0.wireOp",EDGE,"1e7b34f2-0b9f-4ddf-89ed-3da1b662023f.0.6.15"),sQuery(id+"F0.wireOp",EDGE,"1e7b34f2-0b9f-4ddf-89ed-3da1b662023f.0.6.16"),sQuery(id+"F0.wireOp",EDGE,"1e7b34f2-0b9f-4ddf-89ed-3da1b662023f.1.0.1"),sQuery(id+"F0.wireOp",EDGE,"1e7b34f2-0b9f-4ddf-89ed-3da1b662023f.1.0.2"),sQuery(id+"F0.wireOp",EDGE,"1e7b34f2-0b9f-4ddf-89ed-3da1b662023f.1.0.3"),sQuery(id+"F0.wireOp",EDGE,"1e7b34f2-0b9f-4ddf-89ed-3da1b662023f.1.0.4"),sQuery(id+"F0.wireOp",EDGE,"1e7b34f2-0b9f-4ddf-89ed-3da1b662023f.1.0.8"),sQuery(id+"F0.wireOp",EDGE,"1e7b34f2-0b9f-4ddf-89ed-3da1b662023f.1.0.12"),sQuery(id+"F0.wireOp",EDGE,"1e7b34f2-0b9f-4ddf-89ed-3da1b662023f.1.0.13"),sQuery(id+"F0.wireOp",EDGE,"1e7b34f2-0b9f-4ddf-89ed-3da1b662023f.1.0.14"),sQuery(id+"F0.wireOp",EDGE,"1e7b34f2-0b9f-4ddf-89ed-3da1b662023f.1.0.15"),sQuery(id+"F0.wireOp",EDGE,"1e7b34f2-0b9f-4ddf-89ed-3da1b662023f.1.0.16"),sQuery(id+"F0.wireOp",EDGE,"1e7b34f2-0b9f-4ddf-89ed-3da1b662023f.1.1.1"),sQuery(id+"F0.wireOp",EDGE,"1e7b34f2-0b9f-4ddf-89ed-3da1b662023f.1.1.2"),sQuery(id+"F0.wireOp",EDGE,"1e7b34f2-0b9f-4ddf-89ed-3da1b662023f.1.1.3"),sQuery(id+"F0.wireOp",EDGE,"1e7b34f2-0b9f-4ddf-89ed-3da1b662023f.1.1.4"),sQuery(id+"F0.wireOp",EDGE,"1e7b34f2-0b9f-4ddf-89ed-3da1b662023f.1.1.8"),sQuery(id+"F0.wireOp",EDGE,"1e7b34f2-0b9f-4ddf-89ed-3da1b662023f.1.1.12"),sQuery(id+"F0.wireOp",EDGE,"1e7b34f2-0b9f-4ddf-89ed-3da1b662023f.1.1.13"),sQuery(id+"F0.wireOp",EDGE,"1e7b34f2-0b9f-4ddf-89ed-3da1b662023f.1.1.14"),sQuery(id+"F0.wireOp",EDGE,"1e7b34f2-0b9f-4ddf-89ed-3da1b662023f.1.1.15"),sQuery(id+"F0.wireOp",EDGE,"1e7b34f2-0b9f-4ddf-89ed-3da1b662023f.1.1.16"),sQuery(id+"F0.wireOp",EDGE,"1e7b34f2-0b9f-4ddf-89ed-3da1b662023f.1.2.1"),sQuery(id+"F0.wireOp",EDGE,"1e7b34f2-0b9f-4ddf-89ed-3da1b662023f.1.2.2"),sQuery(id+"F0.wireOp",EDGE,"1e7b34f2-0b9f-4ddf-89ed-3da1b662023f.1.2.3"),sQuery(id+"F0.wireOp",EDGE,"1e7b34f2-0b9f-4ddf-89ed-3da1b662023f.1.2.4"),sQuery(id+"F0.wireOp",EDGE,"1e7b34f2-0b9f-4ddf-89ed-3da1b662023f.1.2.8"),sQuery(id+"F0.wireOp",EDGE,"1e7b34f2-0b9f-4ddf-89ed-3da1b662023f.1.2.12"),sQuery(id+"F0.wireOp",EDGE,"1e7b34f2-0b9f-4ddf-89ed-3da1b662023f.1.2.13"),sQuery(id+"F0.wireOp",EDGE,"1e7b34f2-0b9f-4ddf-89ed-3da1b662023f.1.2.14"),sQuery(id+"F0.wireOp",EDGE,"1e7b34f2-0b9f-4ddf-89ed-3da1b662023f.1.2.15"),sQuery(id+"F0.wireOp",EDGE,"1e7b34f2-0b9f-4ddf-89ed-3da1b662023f.1.2.16"),sQuery(id+"F0.wireOp",EDGE,"1e7b34f2-0b9f-4ddf-89ed-3da1b662023f.1.3.1"),sQuery(id+"F0.wireOp",EDGE,"1e7b34f2-0b9f-4ddf-89ed-3da1b662023f.1.3.2"),sQuery(id+"F0.wireOp",EDGE,"1e7b34f2-0b9f-4ddf-89ed-3da1b662023f.1.3.3"),sQuery(id+"F0.wireOp",EDGE,"1e7b34f2-0b9f-4ddf-89ed-3da1b662023f.1.3.4"),sQuery(id+"F0.wireOp",EDGE,"1e7b34f2-0b9f-4ddf-89ed-3da1b662023f.1.3.8"),sQuery(id+"F0.wireOp",EDGE,"1e7b34f2-0b9f-4ddf-89ed-3da1b662023f.1.3.12"),sQuery(id+"F0.wireOp",EDGE,"1e7b34f2-0b9f-4ddf-89ed-3da1b662023f.1.3.13"),sQuery(id+"F0.wireOp",EDGE,"1e7b34f2-0b9f-4ddf-89ed-3da1b662023f.1.3.14"),sQuery(id+"F0.wireOp",EDGE,"1e7b34f2-0b9f-4ddf-89ed-3da1b662023f.1.3.15"),sQuery(id+"F0.wireOp",EDGE,"1e7b34f2-0b9f-4ddf-89ed-3da1b662023f.1.3.16"),sQuery(id+"F0.wireOp",EDGE,"1e7b34f2-0b9f-4ddf-89ed-3da1b662023f.1.4.1"),sQuery(id+"F0.wireOp",EDGE,"1e7b34f2-0b9f-4ddf-89ed-3da1b662023f.1.4.2"),sQuery(id+"F0.wireOp",EDGE,"1e7b34f2-0b9f-4ddf-89ed-3da1b662023f.1.4.3"),sQuery(id+"F0.wireOp",EDGE,"1e7b34f2-0b9f-4ddf-89ed-3da1b662023f.1.4.4"),sQuery(id+"F0.wireOp",EDGE,"1e7b34f2-0b9f-4ddf-89ed-3da1b662023f.1.4.8"),sQuery(id+"F0.wireOp",EDGE,"1e7b34f2-0b9f-4ddf-89ed-3da1b662023f.1.4.12"),sQuery(id+"F0.wireOp",EDGE,"1e7b34f2-0b9f-4ddf-89ed-3da1b662023f.1.4.13"),sQuery(id+"F0.wireOp",EDGE,"1e7b34f2-0b9f-4ddf-89ed-3da1b662023f.1.4.14"),sQuery(id+"F0.wireOp",EDGE,"1e7b34f2-0b9f-4ddf-89ed-3da1b662023f.1.4.15"),sQuery(id+"F0.wireOp",EDGE,"1e7b34f2-0b9f-4ddf-89ed-3da1b662023f.1.4.16"),sQuery(id+"F0.wireOp",EDGE,"1e7b34f2-0b9f-4ddf-89ed-3da1b662023f.1.5.1"),sQuery(id+"F0.wireOp",EDGE,"1e7b34f2-0b9f-4ddf-89ed-3da1b662023f.1.5.2"),sQuery(id+"F0.wireOp",EDGE,"1e7b34f2-0b9f-4ddf-89ed-3da1b662023f.1.5.3"),sQuery(id+"F0.wireOp",EDGE,"1e7b34f2-0b9f-4ddf-89ed-3da1b662023f.1.5.4"),sQuery(id+"F0.wireOp",EDGE,"1e7b34f2-0b9f-4ddf-89ed-3da1b662023f.1.5.8"),sQuery(id+"F0.wireOp",EDGE,"1e7b34f2-0b9f-4ddf-89ed-3da1b662023f.1.5.12"),sQuery(id+"F0.wireOp",EDGE,"1e7b34f2-0b9f-4ddf-89ed-3da1b662023f.1.5.13"),sQuery(id+"F0.wireOp",EDGE,"1e7b34f2-0b9f-4ddf-89ed-3da1b662023f.1.5.14"),sQuery(id+"F0.wireOp",EDGE,"1e7b34f2-0b9f-4ddf-89ed-3da1b662023f.1.5.15"),sQuery(id+"F0.wireOp",EDGE,"1e7b34f2-0b9f-4ddf-89ed-3da1b662023f.1.5.16"),sQuery(id+"F0.wireOp",EDGE,"1e7b34f2-0b9f-4ddf-89ed-3da1b662023f.1.6.1"),sQuery(id+"F0.wireOp",EDGE,"1e7b34f2-0b9f-4ddf-89ed-3da1b662023f.1.6.2"),sQuery(id+"F0.wireOp",EDGE,"1e7b34f2-0b9f-4ddf-89ed-3da1b662023f.1.6.3"),sQuery(id+"F0.wireOp",EDGE,"1e7b34f2-0b9f-4ddf-89ed-3da1b662023f.1.6.4"),sQuery(id+"F0.wireOp",EDGE,"1e7b34f2-0b9f-4ddf-89ed-3da1b662023f.1.6.8"),sQuery(id+"F0.wireOp",EDGE,"1e7b34f2-0b9f-4ddf-89ed-3da1b662023f.1.6.12"),sQuery(id+"F0.wireOp",EDGE,"1e7b34f2-0b9f-4ddf-89ed-3da1b662023f.1.6.13"),sQuery(id+"F0.wireOp",EDGE,"1e7b34f2-0b9f-4ddf-89ed-3da1b662023f.1.6.14"),sQuery(id+"F0.wireOp",EDGE,"1e7b34f2-0b9f-4ddf-89ed-3da1b662023f.1.6.15"),sQuery(id+"F0.wireOp",EDGE,"1e7b34f2-0b9f-4ddf-89ed-3da1b662023f.1.6.16"),sQuery(id+"F0.wireOp",EDGE,"336bbd54-4db4-4eb1-95b0-99f7ab5d0362.1.2.0"),sQuery(id+"F0.wireOp",EDGE,"336bbd54-4db4-4eb1-95b0-99f7ab5d0362.4.2.0"),sQuery(id+"F0.wireOp",EDGE,"336bbd54-4db4-4eb1-95b0-99f7ab5d0362.7.2.0"),sQuery(id+"F0.wireOp",EDGE,"336bbd54-4db4-4eb1-95b0-99f7ab5d0362.9.2.0"),sQuery(id+"F0.wireOp",EDGE,"336bbd54-4db4-4eb1-95b0-99f7ab5d0362.15.2.0"),sQuery(id+"F0.wireOp",EDGE,"336bbd54-4db4-4eb1-95b0-99f7ab5d0362.25.2.0"),sQuery(id+"F0.wireOp",EDGE,"336bbd54-4db4-4eb1-95b0-99f7ab5d0362.27.2.0"),sQuery(id+"F0.wireOp",EDGE,"336bbd54-4db4-4eb1-95b0-99f7ab5d0362.31.2.0"),sQuery(id+"F0.wireOp",EDGE,"336bbd54-4db4-4eb1-95b0-99f7ab5d0362.35.2.0"),sQuery(id+"F0.wireOp",EDGE,"336bbd54-4db4-4eb1-95b0-99f7ab5d0362.39.2.0"),sQuery(id+"F0.wireOp",EDGE,"336bbd54-4db4-4eb1-95b0-99f7ab5d0362.1.2.1"),sQuery(id+"F0.wireOp",EDGE,"336bbd54-4db4-4eb1-95b0-99f7ab5d0362.4.2.1"),sQuery(id+"F0.wireOp",EDGE,"336bbd54-4db4-4eb1-95b0-99f7ab5d0362.7.2.1"),sQuery(id+"F0.wireOp",EDGE,"336bbd54-4db4-4eb1-95b0-99f7ab5d0362.9.2.1"),sQuery(id+"F0.wireOp",EDGE,"336bbd54-4db4-4eb1-95b0-99f7ab5d0362.15.2.1"),sQuery(id+"F0.wireOp",EDGE,"336bbd54-4db4-4eb1-95b0-99f7ab5d0362.25.2.1"),sQuery(id+"F0.wireOp",EDGE,"336bbd54-4db4-4eb1-95b0-99f7ab5d0362.27.2.1"),sQuery(id+"F0.wireOp",EDGE,"336bbd54-4db4-4eb1-95b0-99f7ab5d0362.31.2.1"),sQuery(id+"F0.wireOp",EDGE,"336bbd54-4db4-4eb1-95b0-99f7ab5d0362.35.2.1"),sQuery(id+"F0.wireOp",EDGE,"336bbd54-4db4-4eb1-95b0-99f7ab5d0362.39.2.1"),sQuery(id+"F0.wireOp",EDGE,"336bbd54-4db4-4eb1-95b0-99f7ab5d0362.1.2.2"),sQuery(id+"F0.wireOp",EDGE,"336bbd54-4db4-4eb1-95b0-99f7ab5d0362.4.2.2"),sQuery(id+"F0.wireOp",EDGE,"336bbd54-4db4-4eb1-95b0-99f7ab5d0362.7.2.2"),sQuery(id+"F0.wireOp",EDGE,"336bbd54-4db4-4eb1-95b0-99f7ab5d0362.9.2.2"),sQuery(id+"F0.wireOp",EDGE,"336bbd54-4db4-4eb1-95b0-99f7ab5d0362.15.2.2"),sQuery(id+"F0.wireOp",EDGE,"336bbd54-4db4-4eb1-95b0-99f7ab5d0362.25.2.2"),sQuery(id+"F0.wireOp",EDGE,"336bbd54-4db4-4eb1-95b0-99f7ab5d0362.27.2.2"),sQuery(id+"F0.wireOp",EDGE,"336bbd54-4db4-4eb1-95b0-99f7ab5d0362.31.2.2"),sQuery(id+"F0.wireOp",EDGE,"336bbd54-4db4-4eb1-95b0-99f7ab5d0362.35.2.2"),sQuery(id+"F0.wireOp",EDGE,"336bbd54-4db4-4eb1-95b0-99f7ab5d0362.39.2.2"),sQuery(id+"F0.wireOp",EDGE,"336bbd54-4db4-4eb1-95b0-99f7ab5d0362.1.2.3"),sQuery(id+"F0.wireOp",EDGE,"336bbd54-4db4-4eb1-95b0-99f7ab5d0362.4.2.3"),sQuery(id+"F0.wireOp",EDGE,"336bbd54-4db4-4eb1-95b0-99f7ab5d0362.7.2.3"),sQuery(id+"F0.wireOp",EDGE,"336bbd54-4db4-4eb1-95b0-99f7ab5d0362.9.2.3"),sQuery(id+"F0.wireOp",EDGE,"336bbd54-4db4-4eb1-95b0-99f7ab5d0362.15.2.3"),sQuery(id+"F0.wireOp",EDGE,"336bbd54-4db4-4eb1-95b0-99f7ab5d0362.25.2.3"),sQuery(id+"F0.wireOp",EDGE,"336bbd54-4db4-4eb1-95b0-99f7ab5d0362.27.2.3"),sQuery(id+"F0.wireOp",EDGE,"336bbd54-4db4-4eb1-95b0-99f7ab5d0362.31.2.3"),sQuery(id+"F0.wireOp",EDGE,"336bbd54-4db4-4eb1-95b0-99f7ab5d0362.35.2.3"),sQuery(id+"F0.wireOp",EDGE,"336bbd54-4db4-4eb1-95b0-99f7ab5d0362.39.2.3"),sQuery(id+"F0.wireOp",EDGE,"336bbd54-4db4-4eb1-95b0-99f7ab5d0362.1.2.4"),sQuery(id+"F0.wireOp",EDGE,"336bbd54-4db4-4eb1-95b0-99f7ab5d0362.4.2.4"),sQuery(id+"F0.wireOp",EDGE,"336bbd54-4db4-4eb1-95b0-99f7ab5d0362.7.2.4"),sQuery(id+"F0.wireOp",EDGE,"336bbd54-4db4-4eb1-95b0-99f7ab5d0362.9.2.4"),sQuery(id+"F0.wireOp",EDGE,"336bbd54-4db4-4eb1-95b0-99f7ab5d0362.15.2.4"),sQuery(id+"F0.wireOp",EDGE,"336bbd54-4db4-4eb1-95b0-99f7ab5d0362.25.2.4"),sQuery(id+"F0.wireOp",EDGE,"336bbd54-4db4-4eb1-95b0-99f7ab5d0362.27.2.4"),sQuery(id+"F0.wireOp",EDGE,"336bbd54-4db4-4eb1-95b0-99f7ab5d0362.31.2.4"),sQuery(id+"F0.wireOp",EDGE,"336bbd54-4db4-4eb1-95b0-99f7ab5d0362.35.2.4"),sQuery(id+"F0.wireOp",EDGE,"336bbd54-4db4-4eb1-95b0-99f7ab5d0362.39.2.4"),sQuery(id+"F0.wireOp",EDGE,"336bbd54-4db4-4eb1-95b0-99f7ab5d0362.1.2.5"),sQuery(id+"F0.wireOp",EDGE,"336bbd54-4db4-4eb1-95b0-99f7ab5d0362.4.2.5"),sQuery(id+"F0.wireOp",EDGE,"336bbd54-4db4-4eb1-95b0-99f7ab5d0362.7.2.5"),sQuery(id+"F0.wireOp",EDGE,"336bbd54-4db4-4eb1-95b0-99f7ab5d0362.9.2.5"),sQuery(id+"F0.wireOp",EDGE,"336bbd54-4db4-4eb1-95b0-99f7ab5d0362.15.2.5"),sQuery(id+"F0.wireOp",EDGE,"336bbd54-4db4-4eb1-95b0-99f7ab5d0362.25.2.5"),sQuery(id+"F0.wireOp",EDGE,"336bbd54-4db4-4eb1-95b0-99f7ab5d0362.27.2.5"),sQuery(id+"F0.wireOp",EDGE,"336bbd54-4db4-4eb1-95b0-99f7ab5d0362.31.2.5"),sQuery(id+"F0.wireOp",EDGE,"336bbd54-4db4-4eb1-95b0-99f7ab5d0362.35.2.5"),sQuery(id+"F0.wireOp",EDGE,"336bbd54-4db4-4eb1-95b0-99f7ab5d0362.39.2.5"),sQuery(id+"F0.wireOp",EDGE,"336bbd54-4db4-4eb1-95b0-99f7ab5d0362.1.2.6"),sQuery(id+"F0.wireOp",EDGE,"336bbd54-4db4-4eb1-95b0-99f7ab5d0362.4.2.6"),sQuery(id+"F0.wireOp",EDGE,"336bbd54-4db4-4eb1-95b0-99f7ab5d0362.7.2.6"),sQuery(id+"F0.wireOp",EDGE,"336bbd54-4db4-4eb1-95b0-99f7ab5d0362.9.2.6"),sQuery(id+"F0.wireOp",EDGE,"336bbd54-4db4-4eb1-95b0-99f7ab5d0362.15.2.6"),sQuery(id+"F0.wireOp",EDGE,"336bbd54-4db4-4eb1-95b0-99f7ab5d0362.25.2.6"),sQuery(id+"F0.wireOp",EDGE,"336bbd54-4db4-4eb1-95b0-99f7ab5d0362.27.2.6"),sQuery(id+"F0.wireOp",EDGE,"336bbd54-4db4-4eb1-95b0-99f7ab5d0362.31.2.6"),sQuery(id+"F0.wireOp",EDGE,"336bbd54-4db4-4eb1-95b0-99f7ab5d0362.35.2.6"),sQuery(id+"F0.wireOp",EDGE,"336bbd54-4db4-4eb1-95b0-99f7ab5d0362.39.2.6"),sQuery(id+"F0.wireOp",EDGE,"E3"),sQuery(id+"F0.wireOp",EDGE,"E9.MirrorCS"),sQuery(id+"F0.wireOp",EDGE,"E12.0.1.3"),sQuery(id+"F0.wireOp",EDGE,"E12.0.1.5"),sQuery(id+"F0.wireOp",EDGE,"E12.0.2.3"),sQuery(id+"F0.wireOp",EDGE,"E12.0.2.5"),sQuery(id+"F0.wireOp",EDGE,"E12.1.0.3"),sQuery(id+"F0.wireOp",EDGE,"E12.1.0.5"),sQuery(id+"F0.wireOp",EDGE,"E12.1.1.3"),sQuery(id+"F0.wireOp",EDGE,"E12.1.1.5"),sQuery(id+"F0.wireOp",EDGE,"E12.1.2.3"),sQuery(id+"F0.wireOp",EDGE,"E12.1.2.5"),sQuery(id+"F0.wireOp",EDGE,"E12.2.0.3"),sQuery(id+"F0.wireOp",EDGE,"E12.2.0.5"),sQuery(id+"F0.wireOp",EDGE,"E12.2.1.3"),sQuery(id+"F0.wireOp",EDGE,"E12.2.1.5"),sQuery(id+"F0.wireOp",EDGE,"E12.2.2.3"),sQuery(id+"F0.wireOp",EDGE,"E12.2.2.5")])]});
            hole(context, id + "F2", {"style" : HoleStyle.SIMPLE, "endStyle" : HoleEndStyle.THROUGH, "oppositeDirection" : true, "standardTappedOrClearance" : lookupTablePath({ "standard" : "ANSI", "engagement" : "75%", "pitch" : "32 tpi", "size" : "#6", "type" : "Tapped" }), "standardBlindInLast" : lookupTablePath({ "standard" : "ANSI", "engagement" : "75%", "pitch" : "32 tpi", "size" : "#6", "type" : "Tapped" }), "holeDiameter" : 2.7 * mm, "majorDiameter" : 3.5 * mm, "showTappedDepth" : true, "isTappedThrough" : true, "tappedDepth" : 12.7 * mm, "tapClearance" : 3, "locations" : qUnion([Q0, Q1, Q2, Q3, Q4, Q5, Q6, Q7, Q8, Q9, Q10, Q11, Q12, Q13, Q14, Q15, Q16, Q17, Q18, Q19, Q20, Q21, Q22, Q23, Q24, Q25, Q26, Q27, Q28, Q29, Q30, Q31, Q32, Q33, Q34, Q35]), "scope" : qUnion([Q36])});
        }
        {
            var Q0;
            Q0=sQuery(id+"F0.wireOp",VERTEX,"E32.end");
            var Q1;
            Q1=sQuery(id+"F0.wireOp",VERTEX,"E32.start");
            var Q2;
            Q2=sQuery(id+"F0.wireOp",VERTEX,"E53.10.0.1.start");
            var Q3;
            Q3=sQuery(id+"F0.wireOp",VERTEX,"E53.10.0.1.end");
            var Q4;
            Q4=sQuery(id+"F0.wireOp",VERTEX,"E53.10.0.2.end");
            var Q5;
            Q5=sQuery(id+"F0.wireOp",VERTEX,"E53.10.0.2.start");
            var Q6;
            Q6=sQuery(id+"F0.wireOp",VERTEX,"E53.10.0.3.start");
            var Q7;
            Q7=sQuery(id+"F0.wireOp",VERTEX,"E53.10.0.3.end");
            var Q8;
            Q8=makeQuery(id+"F1.opExtrude","SWEPT_BODY",BODY,{"disambiguationData":[OSD([sQuery(id+"F0.wireOp",EDGE,"E0.bottom"),sQuery(id+"F0.wireOp",EDGE,"E0.top"),sQuery(id+"F0.wireOp",EDGE,"E0.right"),sQuery(id+"F0.wireOp",EDGE,"E3"),sQuery(id+"F0.wireOp",EDGE,"E9.MirrorCS"),sQuery(id+"F0.wireOp",EDGE,"E12.0.1.3"),sQuery(id+"F0.wireOp",EDGE,"E12.0.1.5"),sQuery(id+"F0.wireOp",EDGE,"E12.0.2.3"),sQuery(id+"F0.wireOp",EDGE,"E12.0.2.5"),sQuery(id+"F0.wireOp",EDGE,"E12.1.0.3"),sQuery(id+"F0.wireOp",EDGE,"E12.1.0.5"),sQuery(id+"F0.wireOp",EDGE,"E12.1.1.3"),sQuery(id+"F0.wireOp",EDGE,"E12.1.1.5"),sQuery(id+"F0.wireOp",EDGE,"E12.1.2.3"),sQuery(id+"F0.wireOp",EDGE,"E12.1.2.5"),sQuery(id+"F0.wireOp",EDGE,"E12.2.0.3"),sQuery(id+"F0.wireOp",EDGE,"E12.2.0.5"),sQuery(id+"F0.wireOp",EDGE,"E12.2.1.3"),sQuery(id+"F0.wireOp",EDGE,"E12.2.1.5"),sQuery(id+"F0.wireOp",EDGE,"E12.2.2.3"),sQuery(id+"F0.wireOp",EDGE,"E12.2.2.5"),sQuery(id+"F0.wireOp",EDGE,"E17.0.startCap"),sQuery(id+"F0.wireOp",EDGE,"E17.0.left"),sQuery(id+"F0.wireOp",EDGE,"E17.0.right"),sQuery(id+"F0.wireOp",EDGE,"E18.trimOffspring"),sQuery(id+"F0.wireOp",EDGE,"E19.MirrorCS"),sQuery(id+"F0.wireOp",EDGE,"E20.MirrorCS"),sQuery(id+"F0.wireOp",EDGE,"E21.MirrorCS"),sQuery(id+"F0.wireOp",EDGE,"E22.MirrorCS"),sQuery(id+"F0.wireOp",EDGE,"E23.trimOffspring"),sQuery(id+"F0.wireOp",EDGE,"E24.MirrorCS"),sQuery(id+"F0.wireOp",EDGE,"E25.MirrorCS"),sQuery(id+"F0.wireOp",EDGE,"E26.MirrorCS"),sQuery(id+"F0.wireOp",EDGE,"E27.MirrorCS"),sQuery(id+"F0.wireOp",EDGE,"E28.MirrorCS"),sQuery(id+"F0.wireOp",EDGE,"E29.MirrorCS"),sQuery(id+"F0.wireOp",EDGE,"E30.trimOffspring"),sQuery(id+"F0.wireOp",EDGE,"E31.trimOffspring"),sQuery(id+"F0.wireOp",EDGE,"E36"),sQuery(id+"F0.wireOp",EDGE,"E37"),sQuery(id+"F0.wireOp",EDGE,"E38"),sQuery(id+"F0.wireOp",EDGE,"E39"),sQuery(id+"F0.wireOp",EDGE,"E42"),sQuery(id+"F0.wireOp",EDGE,"E43"),sQuery(id+"F0.wireOp",EDGE,"E44"),sQuery(id+"F0.wireOp",EDGE,"E45"),sQuery(id+"F0.wireOp",EDGE,"E47"),sQuery(id+"F0.wireOp",EDGE,"E48.left"),sQuery(id+"F0.wireOp",EDGE,"E48.right"),sQuery(id+"F0.wireOp",EDGE,"E49.trimOffspring"),sQuery(id+"F0.wireOp",EDGE,"E50.0.1.0"),sQuery(id+"F0.wireOp",EDGE,"E50.0.1.1"),sQuery(id+"F0.wireOp",EDGE,"E50.0.1.3"),sQuery(id+"F0.wireOp",EDGE,"E50.0.1.4"),sQuery(id+"F0.wireOp",EDGE,"E50.0.2.0"),sQuery(id+"F0.wireOp",EDGE,"E50.0.2.1"),sQuery(id+"F0.wireOp",EDGE,"E50.0.2.3"),sQuery(id+"F0.wireOp",EDGE,"E50.0.2.4"),sQuery(id+"F0.wireOp",EDGE,"E50.0.3.0"),sQuery(id+"F0.wireOp",EDGE,"E50.0.3.1"),sQuery(id+"F0.wireOp",EDGE,"E50.0.3.3"),sQuery(id+"F0.wireOp",EDGE,"E50.0.3.4"),sQuery(id+"F0.wireOp",EDGE,"E53.0.0.1"),sQuery(id+"F0.wireOp",EDGE,"E53.3.0.1"),sQuery(id+"F0.wireOp",EDGE,"E53.6.0.1"),sQuery(id+"F0.wireOp",EDGE,"E53.13.0.1"),sQuery(id+"F0.wireOp",EDGE,"E53.16.0.1"),sQuery(id+"F0.wireOp",EDGE,"E53.20.0.1"),sQuery(id+"F0.wireOp",EDGE,"E53.30.0.1"),sQuery(id+"F0.wireOp",EDGE,"E53.37.0.1"),sQuery(id+"F0.wireOp",EDGE,"E53.0.0.2"),sQuery(id+"F0.wireOp",EDGE,"E53.3.0.2"),sQuery(id+"F0.wireOp",EDGE,"E53.6.0.2"),sQuery(id+"F0.wireOp",EDGE,"E53.13.0.2"),sQuery(id+"F0.wireOp",EDGE,"E53.16.0.2"),sQuery(id+"F0.wireOp",EDGE,"E53.20.0.2"),sQuery(id+"F0.wireOp",EDGE,"E53.30.0.2"),sQuery(id+"F0.wireOp",EDGE,"E53.37.0.2"),sQuery(id+"F0.wireOp",EDGE,"E53.0.0.3"),sQuery(id+"F0.wireOp",EDGE,"E53.3.0.3"),sQuery(id+"F0.wireOp",EDGE,"E53.6.0.3"),sQuery(id+"F0.wireOp",EDGE,"E53.13.0.3"),sQuery(id+"F0.wireOp",EDGE,"E53.16.0.3"),sQuery(id+"F0.wireOp",EDGE,"E53.20.0.3"),sQuery(id+"F0.wireOp",EDGE,"E53.30.0.3"),sQuery(id+"F0.wireOp",EDGE,"E53.37.0.3"),sQuery(id+"F0.wireOp",EDGE,"E55"),sQuery(id+"F0.wireOp",EDGE,"E56.0.1.0"),sQuery(id+"F0.wireOp",EDGE,"E59.bottom"),sQuery(id+"F0.wireOp",EDGE,"E59.top"),sQuery(id+"F0.wireOp",EDGE,"E59.left"),sQuery(id+"F0.wireOp",EDGE,"E59.right"),sQuery(id+"F0.wireOp",EDGE,"E61.filletArc"),sQuery(id+"F0.wireOp",EDGE,"E62.filletArc"),sQuery(id+"F0.wireOp",EDGE,"E63.filletArc"),sQuery(id+"F0.wireOp",EDGE,"E64.filletArc")])]});
            hole(context, id + "F3", {"style" : HoleStyle.SIMPLE, "endStyle" : HoleEndStyle.THROUGH, "oppositeDirection" : true, "standardTappedOrClearance" : lookupTablePath({ "standard" : "ANSI", "engagement" : "75%", "pitch" : "40 tpi", "size" : "#4", "type" : "Tapped" }), "standardBlindInLast" : lookupTablePath({ "standard" : "ANSI", "engagement" : "75%", "pitch" : "40 tpi", "size" : "#4", "type" : "Tapped" }), "holeDiameter" : 2.26 * mm, "majorDiameter" : 2.84 * mm, "showTappedDepth" : true, "isTappedThrough" : true, "tappedDepth" : 12.7 * mm, "tapClearance" : 3, "locations" : qUnion([Q0, Q1, Q2, Q3, Q4, Q5, Q6, Q7]), "scope" : qUnion([Q8])});
        }
        {
            var Q0;
            Q0=sQuery(id+"F0.wireOp",VERTEX,"E60.end");
            var Q1;
            Q1=sQuery(id+"F0.wireOp",VERTEX,"E60.start");
            var Q2;
            Q2=makeQuery(id+"F1.opExtrude","SWEPT_BODY",BODY,{"disambiguationData":[OSD([sQuery(id+"F0.wireOp",EDGE,"E0.bottom"),sQuery(id+"F0.wireOp",EDGE,"E0.top"),sQuery(id+"F0.wireOp",EDGE,"E0.right"),sQuery(id+"F0.wireOp",EDGE,"E3"),sQuery(id+"F0.wireOp",EDGE,"E9.MirrorCS"),sQuery(id+"F0.wireOp",EDGE,"E12.0.1.3"),sQuery(id+"F0.wireOp",EDGE,"E12.0.1.5"),sQuery(id+"F0.wireOp",EDGE,"E12.0.2.3"),sQuery(id+"F0.wireOp",EDGE,"E12.0.2.5"),sQuery(id+"F0.wireOp",EDGE,"E12.1.0.3"),sQuery(id+"F0.wireOp",EDGE,"E12.1.0.5"),sQuery(id+"F0.wireOp",EDGE,"E12.1.1.3"),sQuery(id+"F0.wireOp",EDGE,"E12.1.1.5"),sQuery(id+"F0.wireOp",EDGE,"E12.1.2.3"),sQuery(id+"F0.wireOp",EDGE,"E12.1.2.5"),sQuery(id+"F0.wireOp",EDGE,"E12.2.0.3"),sQuery(id+"F0.wireOp",EDGE,"E12.2.0.5"),sQuery(id+"F0.wireOp",EDGE,"E12.2.1.3"),sQuery(id+"F0.wireOp",EDGE,"E12.2.1.5"),sQuery(id+"F0.wireOp",EDGE,"E12.2.2.3"),sQuery(id+"F0.wireOp",EDGE,"E12.2.2.5"),sQuery(id+"F0.wireOp",EDGE,"E17.0.startCap"),sQuery(id+"F0.wireOp",EDGE,"E17.0.left"),sQuery(id+"F0.wireOp",EDGE,"E17.0.right"),sQuery(id+"F0.wireOp",EDGE,"E18.trimOffspring"),sQuery(id+"F0.wireOp",EDGE,"E19.MirrorCS"),sQuery(id+"F0.wireOp",EDGE,"E20.MirrorCS"),sQuery(id+"F0.wireOp",EDGE,"E21.MirrorCS"),sQuery(id+"F0.wireOp",EDGE,"E22.MirrorCS"),sQuery(id+"F0.wireOp",EDGE,"E23.trimOffspring"),sQuery(id+"F0.wireOp",EDGE,"E24.MirrorCS"),sQuery(id+"F0.wireOp",EDGE,"E25.MirrorCS"),sQuery(id+"F0.wireOp",EDGE,"E26.MirrorCS"),sQuery(id+"F0.wireOp",EDGE,"E27.MirrorCS"),sQuery(id+"F0.wireOp",EDGE,"E28.MirrorCS"),sQuery(id+"F0.wireOp",EDGE,"E29.MirrorCS"),sQuery(id+"F0.wireOp",EDGE,"E30.trimOffspring"),sQuery(id+"F0.wireOp",EDGE,"E31.trimOffspring"),sQuery(id+"F0.wireOp",EDGE,"E36"),sQuery(id+"F0.wireOp",EDGE,"E37"),sQuery(id+"F0.wireOp",EDGE,"E38"),sQuery(id+"F0.wireOp",EDGE,"E39"),sQuery(id+"F0.wireOp",EDGE,"E42"),sQuery(id+"F0.wireOp",EDGE,"E43"),sQuery(id+"F0.wireOp",EDGE,"E44"),sQuery(id+"F0.wireOp",EDGE,"E45"),sQuery(id+"F0.wireOp",EDGE,"E47"),sQuery(id+"F0.wireOp",EDGE,"E48.left"),sQuery(id+"F0.wireOp",EDGE,"E48.right"),sQuery(id+"F0.wireOp",EDGE,"E49.trimOffspring"),sQuery(id+"F0.wireOp",EDGE,"E50.0.1.0"),sQuery(id+"F0.wireOp",EDGE,"E50.0.1.1"),sQuery(id+"F0.wireOp",EDGE,"E50.0.1.3"),sQuery(id+"F0.wireOp",EDGE,"E50.0.1.4"),sQuery(id+"F0.wireOp",EDGE,"E50.0.2.0"),sQuery(id+"F0.wireOp",EDGE,"E50.0.2.1"),sQuery(id+"F0.wireOp",EDGE,"E50.0.2.3"),sQuery(id+"F0.wireOp",EDGE,"E50.0.2.4"),sQuery(id+"F0.wireOp",EDGE,"E50.0.3.0"),sQuery(id+"F0.wireOp",EDGE,"E50.0.3.1"),sQuery(id+"F0.wireOp",EDGE,"E50.0.3.3"),sQuery(id+"F0.wireOp",EDGE,"E50.0.3.4"),sQuery(id+"F0.wireOp",EDGE,"E53.0.0.1"),sQuery(id+"F0.wireOp",EDGE,"E53.3.0.1"),sQuery(id+"F0.wireOp",EDGE,"E53.6.0.1"),sQuery(id+"F0.wireOp",EDGE,"E53.13.0.1"),sQuery(id+"F0.wireOp",EDGE,"E53.16.0.1"),sQuery(id+"F0.wireOp",EDGE,"E53.20.0.1"),sQuery(id+"F0.wireOp",EDGE,"E53.30.0.1"),sQuery(id+"F0.wireOp",EDGE,"E53.37.0.1"),sQuery(id+"F0.wireOp",EDGE,"E53.0.0.2"),sQuery(id+"F0.wireOp",EDGE,"E53.3.0.2"),sQuery(id+"F0.wireOp",EDGE,"E53.6.0.2"),sQuery(id+"F0.wireOp",EDGE,"E53.13.0.2"),sQuery(id+"F0.wireOp",EDGE,"E53.16.0.2"),sQuery(id+"F0.wireOp",EDGE,"E53.20.0.2"),sQuery(id+"F0.wireOp",EDGE,"E53.30.0.2"),sQuery(id+"F0.wireOp",EDGE,"E53.37.0.2"),sQuery(id+"F0.wireOp",EDGE,"E53.0.0.3"),sQuery(id+"F0.wireOp",EDGE,"E53.3.0.3"),sQuery(id+"F0.wireOp",EDGE,"E53.6.0.3"),sQuery(id+"F0.wireOp",EDGE,"E53.13.0.3"),sQuery(id+"F0.wireOp",EDGE,"E53.16.0.3"),sQuery(id+"F0.wireOp",EDGE,"E53.20.0.3"),sQuery(id+"F0.wireOp",EDGE,"E53.30.0.3"),sQuery(id+"F0.wireOp",EDGE,"E53.37.0.3"),sQuery(id+"F0.wireOp",EDGE,"E55"),sQuery(id+"F0.wireOp",EDGE,"E56.0.1.0"),sQuery(id+"F0.wireOp",EDGE,"E59.bottom"),sQuery(id+"F0.wireOp",EDGE,"E59.top"),sQuery(id+"F0.wireOp",EDGE,"E59.left"),sQuery(id+"F0.wireOp",EDGE,"E59.right"),sQuery(id+"F0.wireOp",EDGE,"E61.filletArc"),sQuery(id+"F0.wireOp",EDGE,"E62.filletArc"),sQuery(id+"F0.wireOp",EDGE,"E63.filletArc"),sQuery(id+"F0.wireOp",EDGE,"E64.filletArc")])]});
            hole(context, id + "F4", {"style" : HoleStyle.SIMPLE, "endStyle" : HoleEndStyle.THROUGH, "oppositeDirection" : true, "standardTappedOrClearance" : lookupTablePath({ "standard" : "ANSI", "engagement" : "75%", "pitch" : "56 tpi", "size" : "#2", "type" : "Tapped" }), "standardBlindInLast" : lookupTablePath({ "standard" : "ANSI", "engagement" : "75%", "pitch" : "56 tpi", "size" : "#2", "type" : "Tapped" }), "holeDiameter" : 1.78 * mm, "majorDiameter" : 2.18 * mm, "showTappedDepth" : true, "isTappedThrough" : true, "tappedDepth" : 12.7 * mm, "tapClearance" : 3, "locations" : qUnion([Q0, Q1]), "scope" : qUnion([Q2])});
        }
        {
            var Q0;
            Q0=sQuery(id+"F0.wireOp",VERTEX,"E56.0.1.3.end");
            var Q1;
            Q1=sQuery(id+"F0.wireOp",VERTEX,"E56.0.1.2.end");
            var Q2;
            Q2=sQuery(id+"F0.wireOp",VERTEX,"E56.0.1.2.start");
            var Q3;
            Q3=sQuery(id+"F0.wireOp",VERTEX,"E56.0.1.3.start");
            var Q4;
            Q4=sQuery(id+"F0.wireOp",VERTEX,"E54.top.end");
            var Q5;
            Q5=sQuery(id+"F0.wireOp",VERTEX,"E54.top.start");
            var Q6;
            Q6=sQuery(id+"F0.wireOp",VERTEX,"E54.bottom.start");
            var Q7;
            Q7=sQuery(id+"F0.wireOp",VERTEX,"E54.bottom.end");
            var Q8;
            Q8=makeQuery(id+"F1.opExtrude","SWEPT_BODY",BODY,{"disambiguationData":[OSD([sQuery(id+"F0.wireOp",EDGE,"E0.bottom"),sQuery(id+"F0.wireOp",EDGE,"E0.top"),sQuery(id+"F0.wireOp",EDGE,"E0.right"),sQuery(id+"F0.wireOp",EDGE,"E3"),sQuery(id+"F0.wireOp",EDGE,"E9.MirrorCS"),sQuery(id+"F0.wireOp",EDGE,"E12.0.1.3"),sQuery(id+"F0.wireOp",EDGE,"E12.0.1.5"),sQuery(id+"F0.wireOp",EDGE,"E12.0.2.3"),sQuery(id+"F0.wireOp",EDGE,"E12.0.2.5"),sQuery(id+"F0.wireOp",EDGE,"E12.1.0.3"),sQuery(id+"F0.wireOp",EDGE,"E12.1.0.5"),sQuery(id+"F0.wireOp",EDGE,"E12.1.1.3"),sQuery(id+"F0.wireOp",EDGE,"E12.1.1.5"),sQuery(id+"F0.wireOp",EDGE,"E12.1.2.3"),sQuery(id+"F0.wireOp",EDGE,"E12.1.2.5"),sQuery(id+"F0.wireOp",EDGE,"E12.2.0.3"),sQuery(id+"F0.wireOp",EDGE,"E12.2.0.5"),sQuery(id+"F0.wireOp",EDGE,"E12.2.1.3"),sQuery(id+"F0.wireOp",EDGE,"E12.2.1.5"),sQuery(id+"F0.wireOp",EDGE,"E12.2.2.3"),sQuery(id+"F0.wireOp",EDGE,"E12.2.2.5"),sQuery(id+"F0.wireOp",EDGE,"E17.0.startCap"),sQuery(id+"F0.wireOp",EDGE,"E17.0.left"),sQuery(id+"F0.wireOp",EDGE,"E17.0.right"),sQuery(id+"F0.wireOp",EDGE,"E18.trimOffspring"),sQuery(id+"F0.wireOp",EDGE,"E19.MirrorCS"),sQuery(id+"F0.wireOp",EDGE,"E20.MirrorCS"),sQuery(id+"F0.wireOp",EDGE,"E21.MirrorCS"),sQuery(id+"F0.wireOp",EDGE,"E22.MirrorCS"),sQuery(id+"F0.wireOp",EDGE,"E23.trimOffspring"),sQuery(id+"F0.wireOp",EDGE,"E24.MirrorCS"),sQuery(id+"F0.wireOp",EDGE,"E25.MirrorCS"),sQuery(id+"F0.wireOp",EDGE,"E26.MirrorCS"),sQuery(id+"F0.wireOp",EDGE,"E27.MirrorCS"),sQuery(id+"F0.wireOp",EDGE,"E28.MirrorCS"),sQuery(id+"F0.wireOp",EDGE,"E29.MirrorCS"),sQuery(id+"F0.wireOp",EDGE,"E30.trimOffspring"),sQuery(id+"F0.wireOp",EDGE,"E31.trimOffspring"),sQuery(id+"F0.wireOp",EDGE,"E36"),sQuery(id+"F0.wireOp",EDGE,"E37"),sQuery(id+"F0.wireOp",EDGE,"E38"),sQuery(id+"F0.wireOp",EDGE,"E39"),sQuery(id+"F0.wireOp",EDGE,"E42"),sQuery(id+"F0.wireOp",EDGE,"E43"),sQuery(id+"F0.wireOp",EDGE,"E44"),sQuery(id+"F0.wireOp",EDGE,"E45"),sQuery(id+"F0.wireOp",EDGE,"E47"),sQuery(id+"F0.wireOp",EDGE,"E48.left"),sQuery(id+"F0.wireOp",EDGE,"E48.right"),sQuery(id+"F0.wireOp",EDGE,"E49.trimOffspring"),sQuery(id+"F0.wireOp",EDGE,"E50.0.1.0"),sQuery(id+"F0.wireOp",EDGE,"E50.0.1.1"),sQuery(id+"F0.wireOp",EDGE,"E50.0.1.3"),sQuery(id+"F0.wireOp",EDGE,"E50.0.1.4"),sQuery(id+"F0.wireOp",EDGE,"E50.0.2.0"),sQuery(id+"F0.wireOp",EDGE,"E50.0.2.1"),sQuery(id+"F0.wireOp",EDGE,"E50.0.2.3"),sQuery(id+"F0.wireOp",EDGE,"E50.0.2.4"),sQuery(id+"F0.wireOp",EDGE,"E50.0.3.0"),sQuery(id+"F0.wireOp",EDGE,"E50.0.3.1"),sQuery(id+"F0.wireOp",EDGE,"E50.0.3.3"),sQuery(id+"F0.wireOp",EDGE,"E50.0.3.4"),sQuery(id+"F0.wireOp",EDGE,"E53.0.0.1"),sQuery(id+"F0.wireOp",EDGE,"E53.3.0.1"),sQuery(id+"F0.wireOp",EDGE,"E53.6.0.1"),sQuery(id+"F0.wireOp",EDGE,"E53.13.0.1"),sQuery(id+"F0.wireOp",EDGE,"E53.16.0.1"),sQuery(id+"F0.wireOp",EDGE,"E53.20.0.1"),sQuery(id+"F0.wireOp",EDGE,"E53.30.0.1"),sQuery(id+"F0.wireOp",EDGE,"E53.37.0.1"),sQuery(id+"F0.wireOp",EDGE,"E53.0.0.2"),sQuery(id+"F0.wireOp",EDGE,"E53.3.0.2"),sQuery(id+"F0.wireOp",EDGE,"E53.6.0.2"),sQuery(id+"F0.wireOp",EDGE,"E53.13.0.2"),sQuery(id+"F0.wireOp",EDGE,"E53.16.0.2"),sQuery(id+"F0.wireOp",EDGE,"E53.20.0.2"),sQuery(id+"F0.wireOp",EDGE,"E53.30.0.2"),sQuery(id+"F0.wireOp",EDGE,"E53.37.0.2"),sQuery(id+"F0.wireOp",EDGE,"E53.0.0.3"),sQuery(id+"F0.wireOp",EDGE,"E53.3.0.3"),sQuery(id+"F0.wireOp",EDGE,"E53.6.0.3"),sQuery(id+"F0.wireOp",EDGE,"E53.13.0.3"),sQuery(id+"F0.wireOp",EDGE,"E53.16.0.3"),sQuery(id+"F0.wireOp",EDGE,"E53.20.0.3"),sQuery(id+"F0.wireOp",EDGE,"E53.30.0.3"),sQuery(id+"F0.wireOp",EDGE,"E53.37.0.3"),sQuery(id+"F0.wireOp",EDGE,"E55"),sQuery(id+"F0.wireOp",EDGE,"E56.0.1.0"),sQuery(id+"F0.wireOp",EDGE,"E59.bottom"),sQuery(id+"F0.wireOp",EDGE,"E59.top"),sQuery(id+"F0.wireOp",EDGE,"E59.left"),sQuery(id+"F0.wireOp",EDGE,"E59.right"),sQuery(id+"F0.wireOp",EDGE,"E61.filletArc"),sQuery(id+"F0.wireOp",EDGE,"E62.filletArc"),sQuery(id+"F0.wireOp",EDGE,"E63.filletArc"),sQuery(id+"F0.wireOp",EDGE,"E64.filletArc")])]});
            hole(context, id + "F5", {"style" : HoleStyle.SIMPLE, "endStyle" : HoleEndStyle.THROUGH, "oppositeDirection" : true, "standardTappedOrClearance" : lookupTablePath({ "standard" : "ANSI", "engagement" : "75%", "pitch" : "32 tpi", "size" : "#6", "type" : "Tapped" }), "standardBlindInLast" : lookupTablePath({ "standard" : "ANSI", "engagement" : "75%", "pitch" : "32 tpi", "size" : "#6", "type" : "Tapped" }), "holeDiameter" : 2.7 * mm, "majorDiameter" : 3.5 * mm, "showTappedDepth" : true, "isTappedThrough" : true, "tappedDepth" : 12.7 * mm, "tapClearance" : 3, "locations" : qUnion([Q0, Q1, Q2, Q3, Q4, Q5, Q6, Q7]), "scope" : qUnion([Q8])});
        }
    });
